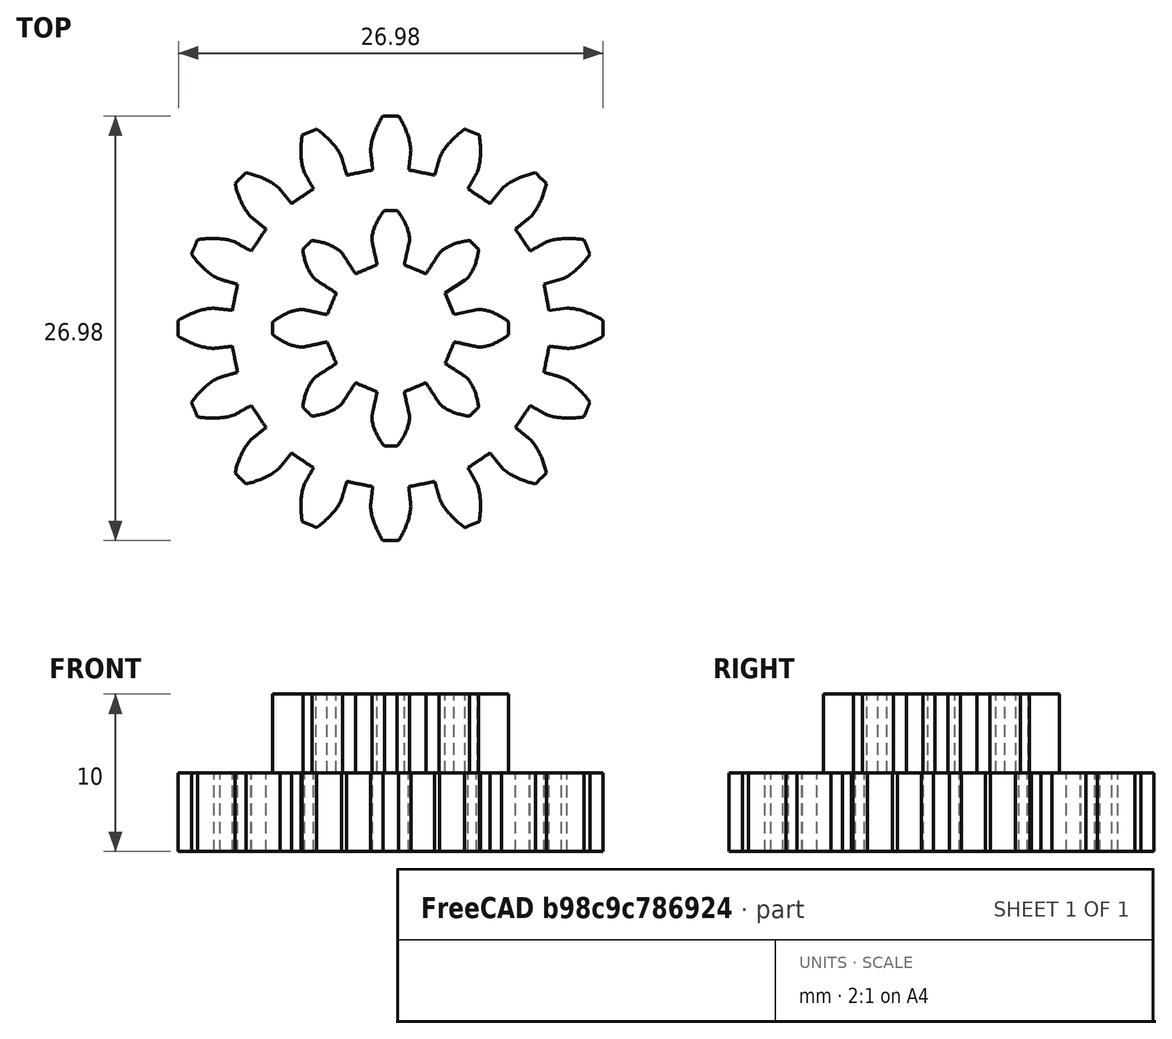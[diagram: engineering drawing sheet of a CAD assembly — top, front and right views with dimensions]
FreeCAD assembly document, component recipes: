
FREECAD ASSEMBLY — COMPONENT RECIPES ("smart_medication_box")

This assembly document has 6 components, labeled P0..P5 below (a component is one placed body or linked part). 6 of them carry a construction recipe — the FreeCAD feature program that regenerates the part from scratch, quoted from this document or its linked companion documents; the rest are supplied as boundary geometry only. No exploded tour is included for this assembly.
COMPONENT P0 — recipe-attached ("base", modeled in this document).
Construction recipe (the document's own serialized feature program — sketch geometry with constraints, then the solid features built on it; lengths are millimeters unless a unit is written):

FEATURE [Sketcher::SketchObject] Sketch003
  ArcFitTolerance = 1e-06
  AttachmentSupport = -> [Origin006]
  ExternalTypes = [0]
  FullyConstrained = true
  MakeInternals = false
  MapMode = 5
  expr: Constraints[0] = 53 * 2
  sketch-geometry (1):
    g0: Circle CenterX=0 CenterY=0 CenterZ=0 NormalX=0 NormalY=0 NormalZ=1 AngleXU=0 Radius=53
  constraints (2):
    c: Diameter(g0) = 106
    c: Coincident(g0,g-1)
FEATURE [PartDesign::Pad] Pad
  Direction = (0,0,1)
  Length = 6
  Length2 = 10
  Profile = -> Sketch003
  ReferenceAxis = -> Sketch003 [N_Axis]
  Refine = true
  SideType = 0
  Suppressed = false
  Type = 0
  Type2 = 0
  expr: Length = 6
FEATURE [Sketcher::SketchObject] Sketch004
  ArcFitTolerance = 1e-06
  AttachmentSupport = -> [Pad]
  ExternalTypes = [0]
  FullyConstrained = true
  MakeInternals = false
  MapMode = 5
  Placement = pos=(0,0,6) rot=(0,0,1;0rad)
  expr: Constraints[0] = 48 * 2 - 4
  sketch-geometry (1):
    g0: Circle CenterX=0 CenterY=0 CenterZ=0 NormalX=0 NormalY=0 NormalZ=1 AngleXU=0 Radius=46
  constraints (2):
    c: Diameter(g0) = 92
    c: Coincident(g0,g-1)
FEATURE [PartDesign::Pad] Pad001
  BaseFeature = -> Pad
  Direction = (0,0,1)
  Length = 6
  Length2 = 10
  Profile = -> Sketch004
  ReferenceAxis = -> Sketch004 [N_Axis]
  Refine = true
  SideType = 0
  Suppressed = false
  Type = 0
  Type2 = 0
  expr: Length = 6
FEATURE [Sketcher::SketchObject] Sketch005
  ArcFitTolerance = 1e-06
  AttachmentSupport = -> [Pad001]
  ExternalGeometry = -> [Pad001]
  ExternalTypes = [0]
  FullyConstrained = true
  MakeInternals = false
  MapMode = 5
  Placement = pos=(0,0,12) rot=(0,0,1;0rad)
  expr: Constraints[0] = 28
  expr: Constraints[4] = 11.5
  sketch-geometry (2):
    g0: Circle CenterX=34.5 CenterY=0 CenterZ=0 NormalX=0 NormalY=0 NormalZ=1 AngleXU=0 Radius=14
    g1: Circle [constr] CenterX=34.5 CenterY=0 CenterZ=0 NormalX=0 NormalY=0 NormalZ=1 AngleXU=0 Radius=11.5
  constraints (5):
    c: Diameter(g0) = 28
    c: Coincident(g1,g0)
    c: Tangent(g1,g-3)
    c: PointOnObject(g0,g-1)
    c: Distance(g0,g-3) = 11.5
FEATURE [PartDesign::Pocket] Pocket001
  BaseFeature = -> Pad001
  Direction = (0,0,-1)
  Length = 6
  Length2 = 5
  Profile = -> Sketch005
  ReferenceAxis = -> Sketch005 [N_Axis]
  Refine = true
  SideType = 0
  Suppressed = false
  Type = 0
  Type2 = 0
  expr: Length = 6
FEATURE [Sketcher::SketchObject] Sketch006
  ArcFitTolerance = 1e-06
  AttachmentSupport = -> [Pocket001]
  ExternalGeometry = -> [Pocket001]
  ExternalTypes = [0,0]
  FullyConstrained = true
  MakeInternals = false
  MapMode = 5
  Placement = pos=(0,0,6) rot=(0,0,1;0rad)
  sketch-geometry (1):
    g0: Circle CenterX=34.5 CenterY=0 CenterZ=0 NormalX=0 NormalY=0 NormalZ=1 AngleXU=0 Radius=7.6
  constraints (2):
    c: Diameter(g0) = 15.2
    c: Coincident(g0,g-4)
FEATURE [PartDesign::Pocket] Pocket002
  BaseFeature = -> Pocket001
  Direction = (0,0,-1)
  Length = 5
  Length2 = 5
  Profile = -> Sketch006
  ReferenceAxis = -> Sketch006 [N_Axis]
  Refine = true
  SideType = 0
  Suppressed = false
  Type = 0
  Type2 = 0
FEATURE [Sketcher::SketchObject] Sketch007
  ArcFitTolerance = 1e-06
  AttachmentSupport = -> [Pocket002]
  ExternalGeometry = -> [Pocket002]
  ExternalTypes = [0]
  FullyConstrained = true
  MakeInternals = false
  MapMode = 5
  Placement = pos=(0,0,12) rot=(0,0,1;0rad)
  expr: Constraints[0] = 28
  expr: Constraints[2] = -3
  sketch-geometry (1):
    g0: Circle CenterX=15.9 CenterY=0 CenterZ=0 NormalX=0 NormalY=0 NormalZ=1 AngleXU=0 Radius=14
  constraints (3):
    c: Diameter(g0) = 28
    c: PointOnObject(g0,g-1)
    c: Distance(g0,g-3) = -3
FEATURE [PartDesign::Pocket] Pocket003
  BaseFeature = -> Pocket002
  Direction = (0,0,-1)
  Length = 11
  Length2 = 5
  Profile = -> Sketch007
  ReferenceAxis = -> Sketch007 [N_Axis]
  Refine = true
  SideType = 0
  Suppressed = false
  Type = 0
  Type2 = 0
  expr: Length = 11
FEATURE [Part::DatumPlane] DatumPlane001
  AttachmentSupport = -> [Pocket003]
  MapMode = 7
  Placement = pos=(53,0,0) rot=(1,0,0;1.5708rad)
FEATURE [Sketcher::SketchObject] Sketch009
  ArcFitTolerance = 1e-06
  AttachmentSupport = -> [DatumPlane001]
  ExternalTypes = [0]
  FullyConstrained = false
  MakeInternals = false
  MapMode = 5
  Placement = pos=(53,0,0) rot=(1,0,0;1.5708rad)
  expr: Constraints[12] = 2
  expr: Constraints[2] = 6
  expr: Constraints[4] = 25
  sketch-geometry (17):
    g0: LineSegment StartX=0 StartY=0 StartZ=0 EndX=0 EndY=6 EndZ=0
    g1: LineSegment StartX=0 StartY=6 StartZ=0 EndX=24.3276 EndY=6 EndZ=0
    g2: LineSegment StartX=25.4755 StartY=6.47549 StartZ=0 EndX=26.6668 EndY=7.66678 EndZ=0
    g3: LineSegment StartX=27.4713 StartY=8 StartZ=0 EndX=28.4345 EndY=8 EndZ=0
    g4: LineSegment StartX=29 StartY=7.43449 StartZ=0 EndX=29 EndY=6.73331 EndZ=0
    g5: LineSegment StartX=28.4815 StartY=5.48147 StartZ=0 EndX=23.8351 EndY=0.835147 EndZ=0
    g6: LineSegment StartX=0 StartY=0 StartZ=0 EndX=21.8189 EndY=0 EndZ=0
    g7: ArcOfCircle CenterX=28.4345 CenterY=7.43449 CenterZ=0 NormalX=0 NormalY=0 NormalZ=1 AngleXU=0 Radius=0.565506 StartAngle=0 EndAngle=1.5708
    g8: GeomPoint [constr] X=29 Y=8 Z=0
    g9: ArcOfCircle CenterX=27.4713 CenterY=6.8623 CenterZ=0 NormalX=0 NormalY=0 NormalZ=1 AngleXU=0 Radius=1.1377 StartAngle=1.5708 EndAngle=2.35619
    g10: GeomPoint [constr] X=27 Y=8 Z=0
    g11: ArcOfCircle CenterX=27.2296 CenterY=6.73331 CenterZ=0 NormalX=0 NormalY=0 NormalZ=1 AngleXU=0 Radius=1.77037 StartAngle=5.49779 EndAngle=6.28319
    g12: GeomPoint [constr] X=29 Y=6 Z=0
    g13: ArcOfCircle CenterX=24.3276 CenterY=7.62341 CenterZ=0 NormalX=0 NormalY=0 NormalZ=1 AngleXU=0 Radius=1.62341 StartAngle=4.71239 EndAngle=5.49779
    g14: GeomPoint [constr] X=25 Y=6 Z=0
    g15: ArcOfCircle CenterX=21.8189 CenterY=2.85137 CenterZ=0 NormalX=0 NormalY=0 NormalZ=1 AngleXU=0 Radius=2.85137 StartAngle=4.71239 EndAngle=5.49779
    g16: GeomPoint [constr] X=23 Y=0 Z=0
  constraints (33):
    c: Coincident(g-1,g0)
    c: Coincident(g0,g1)
    c: Distance(g0,g0) = 6
    c: PointOnObject(g0,g-2)
    c: DistanceX(g1,g14) = 25
    c: PointOnObject(g16,g-1)
    c: Coincident(g6,g0)
    c: Parallel(g2,g5)
    c: Parallel(g1,g6)
    c: Parallel(g3,g1)
    c: Perpendicular(g3,g4)
    c: PointOnObject(g12,g1)
    c: DistanceY(g12,g8) = 2
    c: PointOnObject(g8,g3)
    c: PointOnObject(g8,g4)
    c: Tangent(g3,g7) = 1.5708
    c: Tangent(g4,g7) = 1.5708
    c: PointOnObject(g10,g2)
    c: PointOnObject(g10,g3)
    c: Tangent(g2,g9) = 1.5708
    c: Tangent(g3,g9) = 1.5708
    c: PointOnObject(g12,g5)
    c: PointOnObject(g12,g4)
    c: Tangent(g5,g11) = 1.5708
    c: Tangent(g4,g11) = 1.5708
    c: PointOnObject(g14,g2)
    c: PointOnObject(g14,g1)
    c: Tangent(g2,g13) = -1.5708
    c: Tangent(g1,g13) = -1.5708
    c: PointOnObject(g16,g5)
    c: PointOnObject(g16,g6)
    c: Tangent(g5,g15) = 1.5708
    c: Tangent(g6,g15) = -1.5708
FEATURE [PartDesign::Revolution] Revolution
  Angle = 360
  Angle2 = 60
  Axis = (1e-16,1e-16,1)
  Base = (0,0,0)
  BaseFeature = -> Pocket003
  Profile = -> Sketch009
  ReferenceAxis = -> Z_Axis003
  Refine = true
  Reversed = true
  Suppressed = false
  Type = 0
FEATURE [PartDesign::Fillet] Fillet
  Base = -> Revolution [Edge27]
  BaseFeature = -> Revolution
  Radius = 1
  Refine = true
  SupportTransform = false
  Suppressed = false
  UseAllEdges = false
FEATURE [Sketcher::SketchObject] Sketch019
  ArcFitTolerance = 1e-06
  AttachmentSupport = -> [Fillet]
  ExternalTypes = [0]
  FullyConstrained = true
  MakeInternals = false
  MapMode = 5
  Placement = pos=(0,0,12) rot=(0,0,1;0rad)
  sketch-geometry (1):
    g0: Circle CenterX=0 CenterY=0 CenterZ=0 NormalX=0 NormalY=0 NormalZ=1 AngleXU=0 Radius=44
  constraints (2):
    c: Diameter(g0) = 88
    c: Coincident(g0,g-1)
FEATURE [Part::DatumPlane] DatumPlane005
  AttachmentSupport = -> [Sketch019]
  MapMode = 7
  Placement = pos=(44,0,12) rot=(1,0,0;1.5708rad)
FEATURE [Sketcher::SketchObject] Sketch020
  ArcFitTolerance = 1e-06
  AttachmentSupport = -> [DatumPlane005]
  ExternalTypes = [0]
  FullyConstrained = true
  MakeInternals = false
  MapMode = 5
  Placement = pos=(44,0,12) rot=(1,0,0;1.5708rad)
  sketch-geometry (9):
    g0: LineSegment StartX=-2.19203 StartY=0 StartZ=0 EndX=-2.19203 EndY=3.1 EndZ=0
    g1: LineSegment StartX=-2.19203 StartY=3.1 StartZ=0 EndX=0 EndY=5.29203 EndZ=0
    g2: LineSegment StartX=0 StartY=5.29203 StartZ=0 EndX=0 EndY=7.79203 EndZ=0
    g3: LineSegment StartX=-5.9535 StartY=0 StartZ=0 EndX=-2.19203 EndY=0 EndZ=0
    g4: LineSegment StartX=0 StartY=7.79203 StartZ=0 EndX=-3.44203 EndY=4.35 EndZ=0
    g5: LineSegment StartX=-3.44203 StartY=4.35 StartZ=0 EndX=-5.9535 EndY=0 EndZ=0
    g6: LineSegment [constr] StartX=-3.44203 StartY=4.35 StartZ=0 EndX=-2.19203 EndY=3.1 EndZ=0
    g7: LineSegment StartX=-2.19203 StartY=0 StartZ=0 EndX=0 EndY=0 EndZ=0
    g8: LineSegment StartX=0 StartY=0 StartZ=0 EndX=0 EndY=5.29203 EndZ=0
  constraints (24):
    c: PointOnObject(g0,g-1)
    c: Vertical(g0)
    c: Coincident(g0,g1)
    c: PointOnObject(g1,g-2)
    c: Coincident(g1,g2)
    c: Coincident(g3,g0)
    c: PointOnObject(g3,g-1)
    c: PointOnObject(g2,g-2)
    c: Angle(g1,g0) = 0.785398
    c: DistanceY(g0,g0) = 3.1
    c: Equal(g1,g0)
    c: DistanceY(g2,g2) = 2.5
    c: Coincident(g2,g4)
    c: Coincident(g4,g5)
    c: Coincident(g3,g5)
    c: Angle(g3,g5) = 1.0472
    c: Parallel(g4,g1)
    c: Coincident(g6,g4)
    c: Coincident(g6,g0)
    c: Perpendicular(g4,g6)
    c: Coincident(g7,g0)
    c: Coincident(g7,g-1)
    c: Coincident(g8,g7)
    c: Coincident(g8,g1)
FEATURE [PartDesign::Revolution] Revolution005
  Angle = 323
  Angle2 = 47
  Axis = (1e-16,1e-16,1)
  Base = (0,0,0)
  BaseFeature = -> Fillet
  Profile = -> Sketch020 [Edge4,Edge5,Edge2,Edge1,Edge3,Edge6]
  ReferenceAxis = -> Z_Axis003
  Refine = true
  Reversed = true
  Suppressed = false
  Type = 4
  expr: Angle = 323
  expr: Angle2 = 47
FEATURE [PartDesign::Revolution] Revolution006
  Angle = 313
  Angle2 = 53
  Axis = (1e-16,1e-16,1)
  Base = (0,0,0)
  BaseFeature = -> Revolution005
  Profile = -> Sketch020 [Edge8,Edge3,Edge4,Edge5,Edge6,Edge7]
  ReferenceAxis = -> Z_Axis003
  Refine = true
  Reversed = true
  Suppressed = false
  Type = 4
  expr: Angle = 313
  expr: Angle2 = 53
FEATURE [PartDesign::PolarPattern] PolarPattern004
  Angle = 360
  Axis = -> Z_Axis003
  BaseFeature = -> Revolution006
  Mode = 0
  Occurrences = 4
  Offset = 120
  Originals = -> [Revolution005,Revolution006]
  Refine = true
  Suppressed = false
  TransformMode = 0
  expr: Occurrences = 4
FEATURE [PartDesign::Fillet] Fillet005
  Base = -> PolarPattern004 [Face58,Face22]
  BaseFeature = -> PolarPattern004
  Radius = 0.5
  Refine = true
  SupportTransform = false
  Suppressed = false
  UseAllEdges = false
  expr: Radius = 0.5
FEATURE [PartDesign::Fillet] Fillet006
  Base = -> Fillet005 [Face21,Face18]
  BaseFeature = -> Fillet005
  Radius = 0.5
  Refine = true
  SupportTransform = false
  Suppressed = false
  UseAllEdges = false
  expr: Radius = 0.5
FEATURE [PartDesign::Fillet] Fillet007
  Base = -> Fillet006 [Face29,Face32]
  BaseFeature = -> Fillet006
  Radius = 0.5
  Refine = true
  SupportTransform = false
  Suppressed = false
  UseAllEdges = false
FEATURE [PartDesign::Fillet] Fillet008
  Base = -> Fillet007 [Face44,Face41]
  BaseFeature = -> Fillet007
  Radius = 0.5
  Refine = true
  SupportTransform = false
  Suppressed = false
  UseAllEdges = false
FEATURE [PartDesign::Body] Body003
  AllowCompound = false
  Group = -> [Sketch003,Pad,Sketch004,Pad001,Sketch005,Pocket001,Sketch006,Pocket002,Sketch007,Pocket003,DatumPlane001,Sketch009,Revolution,Fillet,Sketch019,DatumPlane005,Sketch020,Revolution005,Revolution006,PolarPattern004,Fillet005,Fillet006,Fillet007,Fillet008]
  Origin = -> Origin006
  Tip = -> Fillet008
COMPONENT P1 — recipe-attached ("middle_gear", modeled in this document).
Construction recipe (the document's own serialized feature program — sketch geometry with constraints, then the solid features built on it; lengths are millimeters unless a unit is written):

FEATURE [PartDesign::Boolean] Boolean
  Group = -> [InvoluteGear003,InvoluteGear002,Body017]
  Suppressed = false
  Type = 0
  UsePlacement = true
FEATURE [PartDesign::Fillet] Fillet001
  Base = -> Boolean [Face4]
  BaseFeature = -> Boolean
  Radius = 0.25
  Refine = true
  SupportTransform = false
  Suppressed = false
  UseAllEdges = false
  expr: Radius = 0.25
FEATURE [PartDesign::Fillet] Fillet002
  Base = -> Fillet001 [Face4,Face243]
  BaseFeature = -> Fillet001
  Radius = 0.2
  Refine = true
  SupportTransform = false
  Suppressed = false
  UseAllEdges = false
  expr: Radius = 0.2
FEATURE [PartDesign::Body] Body018
  AllowCompound = false
  Group = -> [Boolean,Fillet001,Fillet002]
  Origin = -> Origin030
  Tip = -> Fillet002
COMPONENT P2 — recipe-attached ("desc_upper_ring", modeled in this document).
Construction recipe (the document's own serialized feature program — sketch geometry with constraints, then the solid features built on it; lengths are millimeters unless a unit is written):

FEATURE [Sketcher::SketchObject] Sketch021
  ArcFitTolerance = 1e-06
  AttachmentSupport = -> [Origin036]
  ExternalTypes = [0]
  FullyConstrained = true
  MakeInternals = false
  MapMode = 5
  expr: Constraints[2] = 42.75 * 2
  expr: Constraints[3] = 51 * 2
  sketch-geometry (2):
    g0: Circle CenterX=0 CenterY=0 CenterZ=0 NormalX=0 NormalY=0 NormalZ=1 AngleXU=0 Radius=42.75
    g1: Circle CenterX=0 CenterY=0 CenterZ=0 NormalX=0 NormalY=0 NormalZ=1 AngleXU=0 Radius=51
  constraints (4):
    c: Coincident(g0,g-1)
    c: Coincident(g1,g0)
    c: Diameter(g0) = 85.5
    c: Diameter(g1) = 102
FEATURE [PartDesign::Pad] Pad006
  Direction = (0,0,1)
  Length = 3
  Length2 = 10
  Profile = -> Sketch021
  ReferenceAxis = -> Sketch021 [N_Axis]
  Refine = true
  SideType = 0
  Suppressed = false
  Type = 0
  Type2 = 0
  expr: Length = 3
FEATURE [Sketcher::SketchObject] Sketch022
  ArcFitTolerance = 1e-06
  AttachmentSupport = -> [Pad006]
  ExternalTypes = [0]
  FullyConstrained = false
  MakeInternals = false
  MapMode = 5
  Placement = pos=(0,0,3) rot=(0,0,1;0rad)
  sketch-geometry (4):
    g0: ArcOfCircle CenterX=0 CenterY=0 CenterZ=0 NormalX=0 NormalY=0 NormalZ=1 AngleXU=0 Radius=44.0776 StartAngle=1.01451 EndAngle=1.42895
    g1: ArcOfCircle CenterX=0 CenterY=0 CenterZ=0 NormalX=0 NormalY=0 NormalZ=1 AngleXU=0 Radius=50.0776 StartAngle=1.01451 EndAngle=1.42895
    g2: LineSegment StartX=6.23147 StartY=43.6349 StartZ=0 EndX=7.07972 EndY=49.5746 EndZ=0
    g3: LineSegment StartX=23.2744 StartY=37.4317 StartZ=0 EndX=26.4426 EndY=42.5271 EndZ=0
  constraints (8):
    c: Coincident(g1,g0)
    c: Coincident(g2,g0)
    c: Coincident(g2,g1)
    c: Coincident(g3,g0)
    c: Coincident(g3,g1)
    c: Equal(g2,g3)
    c: Perpendicular(g0,g2)
    c: Distance(g3,g3) = 6
FEATURE [PartDesign::Pocket] Pocket006
  BaseFeature = -> Pad006
  Direction = (0,0,-1)
  Length = 1.5
  Length2 = 5
  Profile = -> Sketch022
  ReferenceAxis = -> Sketch022 [N_Axis]
  Refine = true
  SideType = 0
  Suppressed = false
  Type = 0
  Type2 = 0
  expr: Length = 1.5
FEATURE [PartDesign::PolarPattern] PolarPattern005
  Angle = 360
  Axis = -> Sketch022 [N_Axis]
  BaseFeature = -> Pocket006
  Mode = 0
  Occurrences = 2
  Offset = 120
  Originals = -> [Pocket006]
  Refine = true
  Suppressed = false
  TransformMode = 0
FEATURE [PartDesign::Fillet] Fillet010
  Base = -> PolarPattern005 [Face2]
  BaseFeature = -> PolarPattern005
  Radius = 0.3
  Refine = true
  SupportTransform = false
  Suppressed = false
  UseAllEdges = false
  expr: Radius = 0.3
FEATURE [PartDesign::Fillet] Fillet011
  Base = -> Fillet010 [Face3]
  BaseFeature = -> Fillet010
  Radius = 0.4
  Refine = true
  SupportTransform = false
  Suppressed = false
  UseAllEdges = false
  expr: Radius = 0.4
FEATURE [Sketcher::SketchObject] Sketch023
  ArcFitTolerance = 1e-06
  AttachmentSupport = -> [Fillet011]
  ExternalTypes = [0]
  FullyConstrained = false
  MakeInternals = false
  MapMode = 5
  Placement = pos=(0,0,0) rot=(1,0,0;3.14159rad)
  sketch-geometry (1190):
    g0: BSplineCurve PolesCount=2 KnotsCount=2 Degree=1 IsPeriodic=0
    g1: BSplineCurve PolesCount=2 KnotsCount=2 Degree=1 IsPeriodic=0
    g2: BSplineCurve PolesCount=2 KnotsCount=2 Degree=1 IsPeriodic=0
    g3: BSplineCurve PolesCount=2 KnotsCount=2 Degree=1 IsPeriodic=0
    g4: BSplineCurve PolesCount=2 KnotsCount=2 Degree=1 IsPeriodic=0
    g5: BSplineCurve PolesCount=2 KnotsCount=2 Degree=1 IsPeriodic=0
    g6: BSplineCurve PolesCount=2 KnotsCount=2 Degree=1 IsPeriodic=0
    g7: BSplineCurve PolesCount=2 KnotsCount=2 Degree=1 IsPeriodic=0
    g8: BSplineCurve PolesCount=2 KnotsCount=2 Degree=1 IsPeriodic=0
    g9: BSplineCurve PolesCount=2 KnotsCount=2 Degree=1 IsPeriodic=0
    g10: BSplineCurve PolesCount=2 KnotsCount=2 Degree=1 IsPeriodic=0
    g11: BSplineCurve PolesCount=2 KnotsCount=2 Degree=1 IsPeriodic=0
    g12: BSplineCurve PolesCount=2 KnotsCount=2 Degree=1 IsPeriodic=0
    g13: BSplineCurve PolesCount=2 KnotsCount=2 Degree=1 IsPeriodic=0
    g14: BSplineCurve PolesCount=2 KnotsCount=2 Degree=1 IsPeriodic=0
    g15: BSplineCurve PolesCount=2 KnotsCount=2 Degree=1 IsPeriodic=0
    g16: BSplineCurve PolesCount=2 KnotsCount=2 Degree=1 IsPeriodic=0
    g17: BSplineCurve PolesCount=2 KnotsCount=2 Degree=1 IsPeriodic=0
    g18: BSplineCurve PolesCount=2 KnotsCount=2 Degree=1 IsPeriodic=0
    g19: BSplineCurve PolesCount=2 KnotsCount=2 Degree=1 IsPeriodic=0
    g20: BSplineCurve PolesCount=2 KnotsCount=2 Degree=1 IsPeriodic=0
    g21: BSplineCurve PolesCount=2 KnotsCount=2 Degree=1 IsPeriodic=0
    g22: BSplineCurve PolesCount=2 KnotsCount=2 Degree=1 IsPeriodic=0
    g23: BSplineCurve PolesCount=2 KnotsCount=2 Degree=1 IsPeriodic=0
    g24: BSplineCurve PolesCount=2 KnotsCount=2 Degree=1 IsPeriodic=0
    g25: BSplineCurve PolesCount=2 KnotsCount=2 Degree=1 IsPeriodic=0
    g26: BSplineCurve PolesCount=2 KnotsCount=2 Degree=1 IsPeriodic=0
    g27: BSplineCurve PolesCount=2 KnotsCount=2 Degree=1 IsPeriodic=0
    g28: BSplineCurve PolesCount=2 KnotsCount=2 Degree=1 IsPeriodic=0
    g29: BSplineCurve PolesCount=2 KnotsCount=2 Degree=1 IsPeriodic=0
    g30: BSplineCurve PolesCount=2 KnotsCount=2 Degree=1 IsPeriodic=0
    g31: BSplineCurve PolesCount=2 KnotsCount=2 Degree=1 IsPeriodic=0
    g32: BSplineCurve PolesCount=2 KnotsCount=2 Degree=1 IsPeriodic=0
    g33: BSplineCurve PolesCount=2 KnotsCount=2 Degree=1 IsPeriodic=0
    g34: BSplineCurve PolesCount=2 KnotsCount=2 Degree=1 IsPeriodic=0
    g35: BSplineCurve PolesCount=2 KnotsCount=2 Degree=1 IsPeriodic=0
    g36: BSplineCurve PolesCount=2 KnotsCount=2 Degree=1 IsPeriodic=0
    g37: BSplineCurve PolesCount=2 KnotsCount=2 Degree=1 IsPeriodic=0
    g38: BSplineCurve PolesCount=2 KnotsCount=2 Degree=1 IsPeriodic=0
    g39: BSplineCurve PolesCount=2 KnotsCount=2 Degree=1 IsPeriodic=0
    g40: BSplineCurve PolesCount=2 KnotsCount=2 Degree=1 IsPeriodic=0
    g41: BSplineCurve PolesCount=2 KnotsCount=2 Degree=1 IsPeriodic=0
    g42: BSplineCurve PolesCount=2 KnotsCount=2 Degree=1 IsPeriodic=0
    g43: BSplineCurve PolesCount=2 KnotsCount=2 Degree=1 IsPeriodic=0
    g44: BSplineCurve PolesCount=2 KnotsCount=2 Degree=1 IsPeriodic=0
    g45: BSplineCurve PolesCount=2 KnotsCount=2 Degree=1 IsPeriodic=0
    g46: BSplineCurve PolesCount=2 KnotsCount=2 Degree=1 IsPeriodic=0
    g47: BSplineCurve PolesCount=2 KnotsCount=2 Degree=1 IsPeriodic=0
    g48: BSplineCurve PolesCount=2 KnotsCount=2 Degree=1 IsPeriodic=0
    g49: BSplineCurve PolesCount=2 KnotsCount=2 Degree=1 IsPeriodic=0
    g50: BSplineCurve PolesCount=2 KnotsCount=2 Degree=1 IsPeriodic=0
    g51: BSplineCurve PolesCount=2 KnotsCount=2 Degree=1 IsPeriodic=0
    g52: BSplineCurve PolesCount=2 KnotsCount=2 Degree=1 IsPeriodic=0
    g53: BSplineCurve PolesCount=2 KnotsCount=2 Degree=1 IsPeriodic=0
    g54: BSplineCurve PolesCount=2 KnotsCount=2 Degree=1 IsPeriodic=0
    g55: BSplineCurve PolesCount=2 KnotsCount=2 Degree=1 IsPeriodic=0
    g56: BSplineCurve PolesCount=2 KnotsCount=2 Degree=1 IsPeriodic=0
    g57: BSplineCurve PolesCount=2 KnotsCount=2 Degree=1 IsPeriodic=0
    g58: BSplineCurve PolesCount=2 KnotsCount=2 Degree=1 IsPeriodic=0
    g59: BSplineCurve PolesCount=2 KnotsCount=2 Degree=1 IsPeriodic=0
    g60: BSplineCurve PolesCount=2 KnotsCount=2 Degree=1 IsPeriodic=0
    g61: BSplineCurve PolesCount=2 KnotsCount=2 Degree=1 IsPeriodic=0
    g62: BSplineCurve PolesCount=2 KnotsCount=2 Degree=1 IsPeriodic=0
    g63: BSplineCurve PolesCount=2 KnotsCount=2 Degree=1 IsPeriodic=0
    g64: BSplineCurve PolesCount=2 KnotsCount=2 Degree=1 IsPeriodic=0
    g65: BSplineCurve PolesCount=2 KnotsCount=2 Degree=1 IsPeriodic=0
    g66: BSplineCurve PolesCount=2 KnotsCount=2 Degree=1 IsPeriodic=0
    g67: BSplineCurve PolesCount=2 KnotsCount=2 Degree=1 IsPeriodic=0
    g68: BSplineCurve PolesCount=2 KnotsCount=2 Degree=1 IsPeriodic=0
    g69: BSplineCurve PolesCount=2 KnotsCount=2 Degree=1 IsPeriodic=0
    g70: BSplineCurve PolesCount=2 KnotsCount=2 Degree=1 IsPeriodic=0
    g71: BSplineCurve PolesCount=2 KnotsCount=2 Degree=1 IsPeriodic=0
    g72: BSplineCurve PolesCount=2 KnotsCount=2 Degree=1 IsPeriodic=0
    g73: BSplineCurve PolesCount=2 KnotsCount=2 Degree=1 IsPeriodic=0
    g74: BSplineCurve PolesCount=2 KnotsCount=2 Degree=1 IsPeriodic=0
    g75: BSplineCurve PolesCount=2 KnotsCount=2 Degree=1 IsPeriodic=0
    g76: BSplineCurve PolesCount=2 KnotsCount=2 Degree=1 IsPeriodic=0
    g77: BSplineCurve PolesCount=2 KnotsCount=2 Degree=1 IsPeriodic=0
    g78: BSplineCurve PolesCount=2 KnotsCount=2 Degree=1 IsPeriodic=0
    g79: BSplineCurve PolesCount=2 KnotsCount=2 Degree=1 IsPeriodic=0
    g80: BSplineCurve PolesCount=2 KnotsCount=2 Degree=1 IsPeriodic=0
    g81: BSplineCurve PolesCount=2 KnotsCount=2 Degree=1 IsPeriodic=0
    g82: BSplineCurve PolesCount=2 KnotsCount=2 Degree=1 IsPeriodic=0
    g83: BSplineCurve PolesCount=2 KnotsCount=2 Degree=1 IsPeriodic=0
    g84: BSplineCurve PolesCount=2 KnotsCount=2 Degree=1 IsPeriodic=0
    g85: BSplineCurve PolesCount=2 KnotsCount=2 Degree=1 IsPeriodic=0
    g86: BSplineCurve PolesCount=2 KnotsCount=2 Degree=1 IsPeriodic=0
    g87: BSplineCurve PolesCount=2 KnotsCount=2 Degree=1 IsPeriodic=0
    g88: BSplineCurve PolesCount=2 KnotsCount=2 Degree=1 IsPeriodic=0
    g89: BSplineCurve PolesCount=2 KnotsCount=2 Degree=1 IsPeriodic=0
    g90: BSplineCurve PolesCount=2 KnotsCount=2 Degree=1 IsPeriodic=0
    g91: BSplineCurve PolesCount=2 KnotsCount=2 Degree=1 IsPeriodic=0
    g92: BSplineCurve PolesCount=2 KnotsCount=2 Degree=1 IsPeriodic=0
    g93: BSplineCurve PolesCount=2 KnotsCount=2 Degree=1 IsPeriodic=0
    g94: BSplineCurve PolesCount=2 KnotsCount=2 Degree=1 IsPeriodic=0
    g95: BSplineCurve PolesCount=2 KnotsCount=2 Degree=1 IsPeriodic=0
    g96: BSplineCurve PolesCount=2 KnotsCount=2 Degree=1 IsPeriodic=0
    g97: BSplineCurve PolesCount=2 KnotsCount=2 Degree=1 IsPeriodic=0
    g98: BSplineCurve PolesCount=2 KnotsCount=2 Degree=1 IsPeriodic=0
    g99: BSplineCurve PolesCount=2 KnotsCount=2 Degree=1 IsPeriodic=0
    g100: BSplineCurve PolesCount=2 KnotsCount=2 Degree=1 IsPeriodic=0
    g101: BSplineCurve PolesCount=2 KnotsCount=2 Degree=1 IsPeriodic=0
    g102: BSplineCurve PolesCount=2 KnotsCount=2 Degree=1 IsPeriodic=0
    g103: BSplineCurve PolesCount=2 KnotsCount=2 Degree=1 IsPeriodic=0
    g104: BSplineCurve PolesCount=2 KnotsCount=2 Degree=1 IsPeriodic=0
    g105: BSplineCurve PolesCount=2 KnotsCount=2 Degree=1 IsPeriodic=0
    g106: BSplineCurve PolesCount=2 KnotsCount=2 Degree=1 IsPeriodic=0
    g107: BSplineCurve PolesCount=2 KnotsCount=2 Degree=1 IsPeriodic=0
    g108: BSplineCurve PolesCount=2 KnotsCount=2 Degree=1 IsPeriodic=0
    g109: BSplineCurve PolesCount=2 KnotsCount=2 Degree=1 IsPeriodic=0
    g110: BSplineCurve PolesCount=2 KnotsCount=2 Degree=1 IsPeriodic=0
    g111: BSplineCurve PolesCount=2 KnotsCount=2 Degree=1 IsPeriodic=0
    g112: BSplineCurve PolesCount=2 KnotsCount=2 Degree=1 IsPeriodic=0
    g113: BSplineCurve PolesCount=2 KnotsCount=2 Degree=1 IsPeriodic=0
    g114: BSplineCurve PolesCount=2 KnotsCount=2 Degree=1 IsPeriodic=0
    g115: BSplineCurve PolesCount=2 KnotsCount=2 Degree=1 IsPeriodic=0
    g116: BSplineCurve PolesCount=2 KnotsCount=2 Degree=1 IsPeriodic=0
    g117: BSplineCurve PolesCount=2 KnotsCount=2 Degree=1 IsPeriodic=0
    g118: BSplineCurve PolesCount=2 KnotsCount=2 Degree=1 IsPeriodic=0
    g119: BSplineCurve PolesCount=2 KnotsCount=2 Degree=1 IsPeriodic=0
    g120: BSplineCurve PolesCount=2 KnotsCount=2 Degree=1 IsPeriodic=0
    g121: BSplineCurve PolesCount=2 KnotsCount=2 Degree=1 IsPeriodic=0
    g122: BSplineCurve PolesCount=2 KnotsCount=2 Degree=1 IsPeriodic=0
    g123: BSplineCurve PolesCount=2 KnotsCount=2 Degree=1 IsPeriodic=0
    g124: BSplineCurve PolesCount=2 KnotsCount=2 Degree=1 IsPeriodic=0
    g125: BSplineCurve PolesCount=2 KnotsCount=2 Degree=1 IsPeriodic=0
    g126: BSplineCurve PolesCount=2 KnotsCount=2 Degree=1 IsPeriodic=0
    g127: BSplineCurve PolesCount=2 KnotsCount=2 Degree=1 IsPeriodic=0
    g128: BSplineCurve PolesCount=3 KnotsCount=2 Degree=2 IsPeriodic=0
    g129: BSplineCurve PolesCount=3 KnotsCount=2 Degree=2 IsPeriodic=0
    g130: BSplineCurve PolesCount=3 KnotsCount=2 Degree=2 IsPeriodic=0
    g131: BSplineCurve PolesCount=3 KnotsCount=2 Degree=2 IsPeriodic=0
    g132: BSplineCurve PolesCount=3 KnotsCount=2 Degree=2 IsPeriodic=0
    g133: BSplineCurve PolesCount=3 KnotsCount=2 Degree=2 IsPeriodic=0
    g134: BSplineCurve PolesCount=3 KnotsCount=2 Degree=2 IsPeriodic=0
    g135: BSplineCurve PolesCount=3 KnotsCount=2 Degree=2 IsPeriodic=0
    g136: BSplineCurve PolesCount=3 KnotsCount=2 Degree=2 IsPeriodic=0
    g137: BSplineCurve PolesCount=3 KnotsCount=2 Degree=2 IsPeriodic=0
    g138: BSplineCurve PolesCount=3 KnotsCount=2 Degree=2 IsPeriodic=0
    g139: BSplineCurve PolesCount=3 KnotsCount=2 Degree=2 IsPeriodic=0
    g140: BSplineCurve PolesCount=3 KnotsCount=2 Degree=2 IsPeriodic=0
    g141: BSplineCurve PolesCount=3 KnotsCount=2 Degree=2 IsPeriodic=0
    g142: BSplineCurve PolesCount=3 KnotsCount=2 Degree=2 IsPeriodic=0
    g143: BSplineCurve PolesCount=3 KnotsCount=2 Degree=2 IsPeriodic=0
    g144: BSplineCurve PolesCount=2 KnotsCount=2 Degree=1 IsPeriodic=0
    g145: BSplineCurve PolesCount=2 KnotsCount=2 Degree=1 IsPeriodic=0
    g146: BSplineCurve PolesCount=2 KnotsCount=2 Degree=1 IsPeriodic=0
    g147: BSplineCurve PolesCount=2 KnotsCount=2 Degree=1 IsPeriodic=0
    g148: BSplineCurve PolesCount=2 KnotsCount=2 Degree=1 IsPeriodic=0
    g149: BSplineCurve PolesCount=2 KnotsCount=2 Degree=1 IsPeriodic=0
    g150: BSplineCurve PolesCount=2 KnotsCount=2 Degree=1 IsPeriodic=0
    g151: BSplineCurve PolesCount=2 KnotsCount=2 Degree=1 IsPeriodic=0
    g152: BSplineCurve PolesCount=2 KnotsCount=2 Degree=1 IsPeriodic=0
    g153: BSplineCurve PolesCount=2 KnotsCount=2 Degree=1 IsPeriodic=0
    g154: BSplineCurve PolesCount=2 KnotsCount=2 Degree=1 IsPeriodic=0
    g155: BSplineCurve PolesCount=2 KnotsCount=2 Degree=1 IsPeriodic=0
    g156: BSplineCurve PolesCount=3 KnotsCount=2 Degree=2 IsPeriodic=0
    g157: BSplineCurve PolesCount=3 KnotsCount=2 Degree=2 IsPeriodic=0
    g158: BSplineCurve PolesCount=3 KnotsCount=2 Degree=2 IsPeriodic=0
    g159: BSplineCurve PolesCount=3 KnotsCount=2 Degree=2 IsPeriodic=0
    g160: BSplineCurve PolesCount=3 KnotsCount=2 Degree=2 IsPeriodic=0
    g161: BSplineCurve PolesCount=3 KnotsCount=2 Degree=2 IsPeriodic=0
    g162: BSplineCurve PolesCount=3 KnotsCount=2 Degree=2 IsPeriodic=0
    g163: BSplineCurve PolesCount=3 KnotsCount=2 Degree=2 IsPeriodic=0
    g164: BSplineCurve PolesCount=3 KnotsCount=2 Degree=2 IsPeriodic=0
    g165: BSplineCurve PolesCount=3 KnotsCount=2 Degree=2 IsPeriodic=0
    g166: BSplineCurve PolesCount=2 KnotsCount=2 Degree=1 IsPeriodic=0
    g167: BSplineCurve PolesCount=3 KnotsCount=2 Degree=2 IsPeriodic=0
    g168: BSplineCurve PolesCount=3 KnotsCount=2 Degree=2 IsPeriodic=0
    g169: BSplineCurve PolesCount=3 KnotsCount=2 Degree=2 IsPeriodic=0
    g170: BSplineCurve PolesCount=3 KnotsCount=2 Degree=2 IsPeriodic=0
    g171: BSplineCurve PolesCount=3 KnotsCount=2 Degree=2 IsPeriodic=0
    g172: BSplineCurve PolesCount=3 KnotsCount=2 Degree=2 IsPeriodic=0
    g173: BSplineCurve PolesCount=3 KnotsCount=2 Degree=2 IsPeriodic=0
    g174: BSplineCurve PolesCount=3 KnotsCount=2 Degree=2 IsPeriodic=0
    g175: BSplineCurve PolesCount=3 KnotsCount=2 Degree=2 IsPeriodic=0
    g176: BSplineCurve PolesCount=2 KnotsCount=2 Degree=1 IsPeriodic=0
    g177: BSplineCurve PolesCount=2 KnotsCount=2 Degree=1 IsPeriodic=0
    g178: BSplineCurve PolesCount=2 KnotsCount=2 Degree=1 IsPeriodic=0
    g179: BSplineCurve PolesCount=3 KnotsCount=2 Degree=2 IsPeriodic=0
    g180: BSplineCurve PolesCount=3 KnotsCount=2 Degree=2 IsPeriodic=0
    g181: BSplineCurve PolesCount=3 KnotsCount=2 Degree=2 IsPeriodic=0
    g182: BSplineCurve PolesCount=3 KnotsCount=2 Degree=2 IsPeriodic=0
    g183: BSplineCurve PolesCount=2 KnotsCount=2 Degree=1 IsPeriodic=0
    g184: BSplineCurve PolesCount=3 KnotsCount=2 Degree=2 IsPeriodic=0
    g185: BSplineCurve PolesCount=3 KnotsCount=2 Degree=2 IsPeriodic=0
    g186: BSplineCurve PolesCount=3 KnotsCount=2 Degree=2 IsPeriodic=0
    g187: BSplineCurve PolesCount=3 KnotsCount=2 Degree=2 IsPeriodic=0
    g188: BSplineCurve PolesCount=3 KnotsCount=2 Degree=2 IsPeriodic=0
    g189: BSplineCurve PolesCount=2 KnotsCount=2 Degree=1 IsPeriodic=0
    g190: BSplineCurve PolesCount=2 KnotsCount=2 Degree=1 IsPeriodic=0
    g191: BSplineCurve PolesCount=2 KnotsCount=2 Degree=1 IsPeriodic=0
    g192: BSplineCurve PolesCount=3 KnotsCount=2 Degree=2 IsPeriodic=0
    g193: BSplineCurve PolesCount=3 KnotsCount=2 Degree=2 IsPeriodic=0
    g194: BSplineCurve PolesCount=3 KnotsCount=2 Degree=2 IsPeriodic=0
    g195: BSplineCurve PolesCount=3 KnotsCount=2 Degree=2 IsPeriodic=0
    g196: BSplineCurve PolesCount=3 KnotsCount=2 Degree=2 IsPeriodic=0
    g197: BSplineCurve PolesCount=3 KnotsCount=2 Degree=2 IsPeriodic=0
    g198: BSplineCurve PolesCount=2 KnotsCount=2 Degree=1 IsPeriodic=0
    g199: BSplineCurve PolesCount=3 KnotsCount=2 Degree=2 IsPeriodic=0
    g200: BSplineCurve PolesCount=3 KnotsCount=2 Degree=2 IsPeriodic=0
    g201: BSplineCurve PolesCount=3 KnotsCount=2 Degree=2 IsPeriodic=0
    g202: BSplineCurve PolesCount=3 KnotsCount=2 Degree=2 IsPeriodic=0
    g203: BSplineCurve PolesCount=3 KnotsCount=2 Degree=2 IsPeriodic=0
    g204: BSplineCurve PolesCount=3 KnotsCount=2 Degree=2 IsPeriodic=0
    g205: BSplineCurve PolesCount=2 KnotsCount=2 Degree=1 IsPeriodic=0
    g206: BSplineCurve PolesCount=3 KnotsCount=2 Degree=2 IsPeriodic=0
    g207: BSplineCurve PolesCount=3 KnotsCount=2 Degree=2 IsPeriodic=0
    g208: BSplineCurve PolesCount=2 KnotsCount=2 Degree=1 IsPeriodic=0
    g209: BSplineCurve PolesCount=2 KnotsCount=2 Degree=1 IsPeriodic=0
    g210: BSplineCurve PolesCount=2 KnotsCount=2 Degree=1 IsPeriodic=0
    g211: BSplineCurve PolesCount=2 KnotsCount=2 Degree=1 IsPeriodic=0
    g212: BSplineCurve PolesCount=2 KnotsCount=2 Degree=1 IsPeriodic=0
    g213: BSplineCurve PolesCount=2 KnotsCount=2 Degree=1 IsPeriodic=0
    g214: BSplineCurve PolesCount=2 KnotsCount=2 Degree=1 IsPeriodic=0
    g215: BSplineCurve PolesCount=2 KnotsCount=2 Degree=1 IsPeriodic=0
    g216: BSplineCurve PolesCount=2 KnotsCount=2 Degree=1 IsPeriodic=0
    g217: BSplineCurve PolesCount=2 KnotsCount=2 Degree=1 IsPeriodic=0
    g218: BSplineCurve PolesCount=2 KnotsCount=2 Degree=1 IsPeriodic=0
    g219: BSplineCurve PolesCount=2 KnotsCount=2 Degree=1 IsPeriodic=0
    g220: BSplineCurve PolesCount=2 KnotsCount=2 Degree=1 IsPeriodic=0
    g221: BSplineCurve PolesCount=2 KnotsCount=2 Degree=1 IsPeriodic=0
    g222: BSplineCurve PolesCount=2 KnotsCount=2 Degree=1 IsPeriodic=0
    g223: BSplineCurve PolesCount=2 KnotsCount=2 Degree=1 IsPeriodic=0
    g224: BSplineCurve PolesCount=3 KnotsCount=2 Degree=2 IsPeriodic=0
    g225: BSplineCurve PolesCount=3 KnotsCount=2 Degree=2 IsPeriodic=0
    g226: BSplineCurve PolesCount=3 KnotsCount=2 Degree=2 IsPeriodic=0
    g227: BSplineCurve PolesCount=3 KnotsCount=2 Degree=2 IsPeriodic=0
    g228: BSplineCurve PolesCount=3 KnotsCount=2 Degree=2 IsPeriodic=0
    g229: BSplineCurve PolesCount=3 KnotsCount=2 Degree=2 IsPeriodic=0
    g230: BSplineCurve PolesCount=2 KnotsCount=2 Degree=1 IsPeriodic=0
    g231: BSplineCurve PolesCount=3 KnotsCount=2 Degree=2 IsPeriodic=0
    g232: BSplineCurve PolesCount=3 KnotsCount=2 Degree=2 IsPeriodic=0
    g233: BSplineCurve PolesCount=3 KnotsCount=2 Degree=2 IsPeriodic=0
    g234: BSplineCurve PolesCount=3 KnotsCount=2 Degree=2 IsPeriodic=0
    g235: BSplineCurve PolesCount=3 KnotsCount=2 Degree=2 IsPeriodic=0
    g236: BSplineCurve PolesCount=3 KnotsCount=2 Degree=2 IsPeriodic=0
    g237: BSplineCurve PolesCount=3 KnotsCount=2 Degree=2 IsPeriodic=0
    g238: BSplineCurve PolesCount=2 KnotsCount=2 Degree=1 IsPeriodic=0
    g239: BSplineCurve PolesCount=2 KnotsCount=2 Degree=1 IsPeriodic=0
    g240: BSplineCurve PolesCount=2 KnotsCount=2 Degree=1 IsPeriodic=0
    g241: BSplineCurve PolesCount=2 KnotsCount=2 Degree=1 IsPeriodic=0
    g242: BSplineCurve PolesCount=2 KnotsCount=2 Degree=1 IsPeriodic=0
    g243: BSplineCurve PolesCount=2 KnotsCount=2 Degree=1 IsPeriodic=0
    g244: BSplineCurve PolesCount=3 KnotsCount=2 Degree=2 IsPeriodic=0
    g245: BSplineCurve PolesCount=3 KnotsCount=2 Degree=2 IsPeriodic=0
    g246: BSplineCurve PolesCount=3 KnotsCount=2 Degree=2 IsPeriodic=0
    g247: BSplineCurve PolesCount=3 KnotsCount=2 Degree=2 IsPeriodic=0
    g248: BSplineCurve PolesCount=3 KnotsCount=2 Degree=2 IsPeriodic=0
    g249: BSplineCurve PolesCount=3 KnotsCount=2 Degree=2 IsPeriodic=0
    g250: BSplineCurve PolesCount=3 KnotsCount=2 Degree=2 IsPeriodic=0
    g251: BSplineCurve PolesCount=3 KnotsCount=2 Degree=2 IsPeriodic=0
    g252: BSplineCurve PolesCount=3 KnotsCount=2 Degree=2 IsPeriodic=0
    g253: BSplineCurve PolesCount=3 KnotsCount=2 Degree=2 IsPeriodic=0
    g254: BSplineCurve PolesCount=3 KnotsCount=2 Degree=2 IsPeriodic=0
    g255: BSplineCurve PolesCount=3 KnotsCount=2 Degree=2 IsPeriodic=0
    g256: BSplineCurve PolesCount=3 KnotsCount=2 Degree=2 IsPeriodic=0
    g257: BSplineCurve PolesCount=3 KnotsCount=2 Degree=2 IsPeriodic=0
    g258: BSplineCurve PolesCount=3 KnotsCount=2 Degree=2 IsPeriodic=0
    g259: BSplineCurve PolesCount=3 KnotsCount=2 Degree=2 IsPeriodic=0
    g260: BSplineCurve PolesCount=3 KnotsCount=2 Degree=2 IsPeriodic=0
    g261: BSplineCurve PolesCount=2 KnotsCount=2 Degree=1 IsPeriodic=0
    g262: BSplineCurve PolesCount=3 KnotsCount=2 Degree=2 IsPeriodic=0
    g263: BSplineCurve PolesCount=3 KnotsCount=2 Degree=2 IsPeriodic=0
    g264: BSplineCurve PolesCount=3 KnotsCount=2 Degree=2 IsPeriodic=0
    g265: BSplineCurve PolesCount=3 KnotsCount=2 Degree=2 IsPeriodic=0
    g266: BSplineCurve PolesCount=3 KnotsCount=2 Degree=2 IsPeriodic=0
    g267: BSplineCurve PolesCount=3 KnotsCount=2 Degree=2 IsPeriodic=0
    g268: BSplineCurve PolesCount=3 KnotsCount=2 Degree=2 IsPeriodic=0
    g269: BSplineCurve PolesCount=3 KnotsCount=2 Degree=2 IsPeriodic=0
    g270: BSplineCurve PolesCount=3 KnotsCount=2 Degree=2 IsPeriodic=0
    g271: BSplineCurve PolesCount=3 KnotsCount=2 Degree=2 IsPeriodic=0
    g272: BSplineCurve PolesCount=3 KnotsCount=2 Degree=2 IsPeriodic=0
    g273: BSplineCurve PolesCount=2 KnotsCount=2 Degree=1 IsPeriodic=0
    g274: BSplineCurve PolesCount=3 KnotsCount=2 Degree=2 IsPeriodic=0
    g275: BSplineCurve PolesCount=3 KnotsCount=2 Degree=2 IsPeriodic=0
    g276: BSplineCurve PolesCount=2 KnotsCount=2 Degree=1 IsPeriodic=0
    g277: BSplineCurve PolesCount=2 KnotsCount=2 Degree=1 IsPeriodic=0
    g278: BSplineCurve PolesCount=2 KnotsCount=2 Degree=1 IsPeriodic=0
    g279: BSplineCurve PolesCount=2 KnotsCount=2 Degree=1 IsPeriodic=0
    g280: BSplineCurve PolesCount=3 KnotsCount=2 Degree=2 IsPeriodic=0
    g281: BSplineCurve PolesCount=3 KnotsCount=2 Degree=2 IsPeriodic=0
    g282: BSplineCurve PolesCount=3 KnotsCount=2 Degree=2 IsPeriodic=0
    g283: BSplineCurve PolesCount=3 KnotsCount=2 Degree=2 IsPeriodic=0
    g284: BSplineCurve PolesCount=3 KnotsCount=2 Degree=2 IsPeriodic=0
    g285: BSplineCurve PolesCount=2 KnotsCount=2 Degree=1 IsPeriodic=0
    g286: BSplineCurve PolesCount=3 KnotsCount=2 Degree=2 IsPeriodic=0
    g287: BSplineCurve PolesCount=3 KnotsCount=2 Degree=2 IsPeriodic=0
    g288: BSplineCurve PolesCount=3 KnotsCount=2 Degree=2 IsPeriodic=0
    g289: BSplineCurve PolesCount=3 KnotsCount=2 Degree=2 IsPeriodic=0
    g290: BSplineCurve PolesCount=3 KnotsCount=2 Degree=2 IsPeriodic=0
    g291: BSplineCurve PolesCount=3 KnotsCount=2 Degree=2 IsPeriodic=0
    g292: BSplineCurve PolesCount=2 KnotsCount=2 Degree=1 IsPeriodic=0
    g293: BSplineCurve PolesCount=3 KnotsCount=2 Degree=2 IsPeriodic=0
    g294: BSplineCurve PolesCount=3 KnotsCount=2 Degree=2 IsPeriodic=0
    g295: BSplineCurve PolesCount=3 KnotsCount=2 Degree=2 IsPeriodic=0
    g296: BSplineCurve PolesCount=3 KnotsCount=2 Degree=2 IsPeriodic=0
    g297: BSplineCurve PolesCount=3 KnotsCount=2 Degree=2 IsPeriodic=0
    g298: BSplineCurve PolesCount=3 KnotsCount=2 Degree=2 IsPeriodic=0
    g299: BSplineCurve PolesCount=3 KnotsCount=2 Degree=2 IsPeriodic=0
    g300: BSplineCurve PolesCount=3 KnotsCount=2 Degree=2 IsPeriodic=0
    g301: BSplineCurve PolesCount=3 KnotsCount=2 Degree=2 IsPeriodic=0
    g302: BSplineCurve PolesCount=3 KnotsCount=2 Degree=2 IsPeriodic=0
    g303: BSplineCurve PolesCount=3 KnotsCount=2 Degree=2 IsPeriodic=0
    g304: BSplineCurve PolesCount=3 KnotsCount=2 Degree=2 IsPeriodic=0
    g305: BSplineCurve PolesCount=3 KnotsCount=2 Degree=2 IsPeriodic=0
    g306: BSplineCurve PolesCount=3 KnotsCount=2 Degree=2 IsPeriodic=0
    g307: BSplineCurve PolesCount=3 KnotsCount=2 Degree=2 IsPeriodic=0
    g308: BSplineCurve PolesCount=3 KnotsCount=2 Degree=2 IsPeriodic=0
    g309: BSplineCurve PolesCount=3 KnotsCount=2 Degree=2 IsPeriodic=0
    g310: BSplineCurve PolesCount=3 KnotsCount=2 Degree=2 IsPeriodic=0
    g311: BSplineCurve PolesCount=3 KnotsCount=2 Degree=2 IsPeriodic=0
    g312: BSplineCurve PolesCount=3 KnotsCount=2 Degree=2 IsPeriodic=0
    g313: BSplineCurve PolesCount=3 KnotsCount=2 Degree=2 IsPeriodic=0
    g314: BSplineCurve PolesCount=3 KnotsCount=2 Degree=2 IsPeriodic=0
    g315: BSplineCurve PolesCount=3 KnotsCount=2 Degree=2 IsPeriodic=0
    g316: BSplineCurve PolesCount=3 KnotsCount=2 Degree=2 IsPeriodic=0
    g317: BSplineCurve PolesCount=3 KnotsCount=2 Degree=2 IsPeriodic=0
    g318: BSplineCurve PolesCount=3 KnotsCount=2 Degree=2 IsPeriodic=0
    g319: BSplineCurve PolesCount=3 KnotsCount=2 Degree=2 IsPeriodic=0
    g320: BSplineCurve PolesCount=2 KnotsCount=2 Degree=1 IsPeriodic=0
    g321: BSplineCurve PolesCount=3 KnotsCount=2 Degree=2 IsPeriodic=0
    g322: BSplineCurve PolesCount=3 KnotsCount=2 Degree=2 IsPeriodic=0
    g323: BSplineCurve PolesCount=3 KnotsCount=2 Degree=2 IsPeriodic=0
    g324: BSplineCurve PolesCount=3 KnotsCount=2 Degree=2 IsPeriodic=0
    g325: BSplineCurve PolesCount=3 KnotsCount=2 Degree=2 IsPeriodic=0
    g326: BSplineCurve PolesCount=3 KnotsCount=2 Degree=2 IsPeriodic=0
    g327: BSplineCurve PolesCount=3 KnotsCount=2 Degree=2 IsPeriodic=0
    g328: BSplineCurve PolesCount=3 KnotsCount=2 Degree=2 IsPeriodic=0
    g329: BSplineCurve PolesCount=3 KnotsCount=2 Degree=2 IsPeriodic=0
    g330: BSplineCurve PolesCount=3 KnotsCount=2 Degree=2 IsPeriodic=0
    g331: BSplineCurve PolesCount=3 KnotsCount=2 Degree=2 IsPeriodic=0
    g332: BSplineCurve PolesCount=3 KnotsCount=2 Degree=2 IsPeriodic=0
    g333: BSplineCurve PolesCount=3 KnotsCount=2 Degree=2 IsPeriodic=0
    g334: BSplineCurve PolesCount=3 KnotsCount=2 Degree=2 IsPeriodic=0
    g335: BSplineCurve PolesCount=3 KnotsCount=2 Degree=2 IsPeriodic=0
    g336: BSplineCurve PolesCount=3 KnotsCount=2 Degree=2 IsPeriodic=0
    g337: BSplineCurve PolesCount=2 KnotsCount=2 Degree=1 IsPeriodic=0
    g338: BSplineCurve PolesCount=2 KnotsCount=2 Degree=1 IsPeriodic=0
    g339: BSplineCurve PolesCount=2 KnotsCount=2 Degree=1 IsPeriodic=0
    g340: BSplineCurve PolesCount=2 KnotsCount=2 Degree=1 IsPeriodic=0
    g341: BSplineCurve PolesCount=2 KnotsCount=2 Degree=1 IsPeriodic=0
    g342: BSplineCurve PolesCount=2 KnotsCount=2 Degree=1 IsPeriodic=0
    g343: BSplineCurve PolesCount=2 KnotsCount=2 Degree=1 IsPeriodic=0
    g344: BSplineCurve PolesCount=2 KnotsCount=2 Degree=1 IsPeriodic=0
    g345: BSplineCurve PolesCount=2 KnotsCount=2 Degree=1 IsPeriodic=0
    g346: BSplineCurve PolesCount=2 KnotsCount=2 Degree=1 IsPeriodic=0
    g347: BSplineCurve PolesCount=2 KnotsCount=2 Degree=1 IsPeriodic=0
    g348: BSplineCurve PolesCount=3 KnotsCount=2 Degree=2 IsPeriodic=0
    g349: BSplineCurve PolesCount=3 KnotsCount=2 Degree=2 IsPeriodic=0
    g350: BSplineCurve PolesCount=3 KnotsCount=2 Degree=2 IsPeriodic=0
    g351: BSplineCurve PolesCount=3 KnotsCount=2 Degree=2 IsPeriodic=0
    g352: BSplineCurve PolesCount=3 KnotsCount=2 Degree=2 IsPeriodic=0
    g353: BSplineCurve PolesCount=3 KnotsCount=2 Degree=2 IsPeriodic=0
    g354: BSplineCurve PolesCount=3 KnotsCount=2 Degree=2 IsPeriodic=0
    g355: BSplineCurve PolesCount=3 KnotsCount=2 Degree=2 IsPeriodic=0
    g356: BSplineCurve PolesCount=3 KnotsCount=2 Degree=2 IsPeriodic=0
    g357: BSplineCurve PolesCount=3 KnotsCount=2 Degree=2 IsPeriodic=0
    g358: BSplineCurve PolesCount=3 KnotsCount=2 Degree=2 IsPeriodic=0
    g359: BSplineCurve PolesCount=3 KnotsCount=2 Degree=2 IsPeriodic=0
    g360: BSplineCurve PolesCount=3 KnotsCount=2 Degree=2 IsPeriodic=0
    g361: BSplineCurve PolesCount=3 KnotsCount=2 Degree=2 IsPeriodic=0
    g362: BSplineCurve PolesCount=3 KnotsCount=2 Degree=2 IsPeriodic=0
    g363: BSplineCurve PolesCount=3 KnotsCount=2 Degree=2 IsPeriodic=0
    g364: BSplineCurve PolesCount=2 KnotsCount=2 Degree=1 IsPeriodic=0
    g365: BSplineCurve PolesCount=2 KnotsCount=2 Degree=1 IsPeriodic=0
    g366: BSplineCurve PolesCount=2 KnotsCount=2 Degree=1 IsPeriodic=0
    g367: BSplineCurve PolesCount=2 KnotsCount=2 Degree=1 IsPeriodic=0
    g368: BSplineCurve PolesCount=2 KnotsCount=2 Degree=1 IsPeriodic=0
    g369: BSplineCurve PolesCount=2 KnotsCount=2 Degree=1 IsPeriodic=0
    g370: BSplineCurve PolesCount=2 KnotsCount=2 Degree=1 IsPeriodic=0
    g371: BSplineCurve PolesCount=2 KnotsCount=2 Degree=1 IsPeriodic=0
    g372: BSplineCurve PolesCount=2 KnotsCount=2 Degree=1 IsPeriodic=0
    g373: BSplineCurve PolesCount=2 KnotsCount=2 Degree=1 IsPeriodic=0
    g374: BSplineCurve PolesCount=2 KnotsCount=2 Degree=1 IsPeriodic=0
    g375: BSplineCurve PolesCount=2 KnotsCount=2 Degree=1 IsPeriodic=0
    g376: BSplineCurve PolesCount=2 KnotsCount=2 Degree=1 IsPeriodic=0
    g377: BSplineCurve PolesCount=2 KnotsCount=2 Degree=1 IsPeriodic=0
    g378: BSplineCurve PolesCount=2 KnotsCount=2 Degree=1 IsPeriodic=0
    g379: BSplineCurve PolesCount=2 KnotsCount=2 Degree=1 IsPeriodic=0
    g380: BSplineCurve PolesCount=2 KnotsCount=2 Degree=1 IsPeriodic=0
    g381: BSplineCurve PolesCount=2 KnotsCount=2 Degree=1 IsPeriodic=0
    g382: BSplineCurve PolesCount=2 KnotsCount=2 Degree=1 IsPeriodic=0
    g383: BSplineCurve PolesCount=2 KnotsCount=2 Degree=1 IsPeriodic=0
    g384: BSplineCurve PolesCount=2 KnotsCount=2 Degree=1 IsPeriodic=0
    g385: BSplineCurve PolesCount=2 KnotsCount=2 Degree=1 IsPeriodic=0
    g386: BSplineCurve PolesCount=2 KnotsCount=2 Degree=1 IsPeriodic=0
    g387: BSplineCurve PolesCount=2 KnotsCount=2 Degree=1 IsPeriodic=0
    g388: BSplineCurve PolesCount=2 KnotsCount=2 Degree=1 IsPeriodic=0
    g389: BSplineCurve PolesCount=2 KnotsCount=2 Degree=1 IsPeriodic=0
    g390: BSplineCurve PolesCount=2 KnotsCount=2 Degree=1 IsPeriodic=0
    g391: BSplineCurve PolesCount=2 KnotsCount=2 Degree=1 IsPeriodic=0
    g392: BSplineCurve PolesCount=2 KnotsCount=2 Degree=1 IsPeriodic=0
    g393: BSplineCurve PolesCount=2 KnotsCount=2 Degree=1 IsPeriodic=0
    g394: BSplineCurve PolesCount=2 KnotsCount=2 Degree=1 IsPeriodic=0
    g395: BSplineCurve PolesCount=2 KnotsCount=2 Degree=1 IsPeriodic=0
    g396: BSplineCurve PolesCount=2 KnotsCount=2 Degree=1 IsPeriodic=0
    g397: BSplineCurve PolesCount=2 KnotsCount=2 Degree=1 IsPeriodic=0
    g398: BSplineCurve PolesCount=3 KnotsCount=2 Degree=2 IsPeriodic=0
    g399: BSplineCurve PolesCount=3 KnotsCount=2 Degree=2 IsPeriodic=0
    ... +790 more geometry lines
  constraints (1190):
    c: Coincident(g93,g94)
    c: Coincident(g92,g93)
    c: Coincident(g282,g284)
    c: Coincident(g273,g274)
    c: Coincident(g272,g273)
    c: Coincident(g280,g282)
    c: Coincident(g88,g89)
    c: Coincident(g96,g97)
    c: Coincident(g299,g300)
    c: Coincident(g284,g286)
    c: Coincident(g298,g299)
    c: Coincident(g96,g99)
    c: Coincident(g89,g90)
    c: Coincident(g280,g281)
    c: Coincident(g271,g272)
    c: Coincident(g298,g304)
    c: Coincident(g300,g301)
    c: Coincident(g286,g288)
    c: Coincident(g274,g275)
    c: Coincident(g281,g283)
    c: Coincident(g303,g304)
    c: Coincident(g301,g302)
    c: Coincident(g288,g290)
    c: Coincident(g302,g303)
    c: Coincident(g283,g285)
    c: Coincident(g285,g287)
    c: Coincident(g290,g292)
    c: Coincident(g292,g294)
    c: Coincident(g270,g271)
    c: Coincident(g306,g308)
    c: Coincident(g287,g289)
    c: Coincident(g249,g251)
    c: Coincident(g314,g316)
    c: Coincident(g305,g306)
    c: Coincident(g308,g310)
    c: Coincident(g294,g296)
    c: Coincident(g251,g253)
    c: Coincident(g312,g314)
    c: Coincident(g263,g264)
    c: Coincident(g322,g324)
    c: Coincident(g316,g318)
    c: Coincident(g264,g265)
    c: Coincident(g289,g291)
    c: Coincident(g305,g307)
    c: Coincident(g324,g326)
    c: Coincident(g247,g249)
    c: Coincident(g310,g311)
    c: Coincident(g296,g297)
    c: Coincident(g262,g263)
    c: Coincident(g276,g277)
    c: Coincident(g320,g322)
    c: Coincident(g318,g320)
    c: Coincident(g265,g266)
    c: Coincident(g309,g311)
    c: Coincident(g275,g276)
    c: Coincident(g307,g309)
    c: Coincident(g291,g293)
    c: Coincident(g270,g279)
    c: Coincident(g325,g327)
    c: Coincident(g323,g325)
    c: Coincident(g100,g101)
    c: Coincident(g84,g85)
    c: Coincident(g253,g255)
    c: Coincident(g295,g297)
    c: Coincident(g277,g278)
    c: Coincident(g262,g269)
    c: Coincident(g312,g313)
    c: Coincident(g326,g327)
    c: Coincident(g247,g248)
    c: Coincident(g293,g295)
    c: Coincident(g329,g330)
    c: Coincident(g330,g331)
    c: Coincident(g278,g279)
    c: Coincident(g254,g256)
    c: Coincident(g266,g267)
    c: Coincident(g85,g86)
    c: Coincident(g100,g103)
    c: Coincident(g328,g329)
    c: Coincident(g321,g323)
    c: Coincident(g268,g269)
    c: Coincident(g267,g268)
    c: Coincident(g331,g332)
    c: Coincident(g94,g95)
    c: Coincident(g92,g95)
    c: Coincident(g252,g254)
    c: Coincident(g328,g336)
    c: Coincident(g248,g250)
    c: Coincident(g250,g252)
    c: Coincident(g332,g333)
    c: Coincident(g256,g258)
    c: Coincident(g319,g321)
    c: Coincident(g335,g336)
    c: Coincident(g255,g257)
    c: Coincident(g313,g315)
    c: Coincident(g88,g91)
    c: Coincident(g97,g98)
    c: Coincident(g260,g261)
    c: Coincident(g98,g99)
    c: Coincident(g90,g91)
    c: Coincident(g333,g334)
    c: Coincident(g259,g261)
    c: Coincident(g334,g335)
    c: Coincident(g258,g260)
    c: Coincident(g317,g319)
    c: Coincident(g348,g350)
    c: Coincident(g350,g352)
    c: Coincident(g315,g317)
    c: Coincident(g257,g259)
    c: Coincident(g357,g358)
    c: Coincident(g356,g357)
    c: Coincident(g228,g229)
    c: Coincident(g227,g228)
    c: Coincident(g346,g347)
    c: Coincident(g229,g230)
    c: Coincident(g352,g354)
    c: Coincident(g358,g359)
    c: Coincident(g231,g232)
    c: Coincident(g348,g349)
    c: Coincident(g230,g231)
    c: Coincident(g345,g346)
    c: Coincident(g356,g363)
    c: Coincident(g226,g227)
    c: Coincident(g232,g233)
    c: Coincident(g344,g345)
    c: Coincident(g238,g239)
    c: Coincident(g338,g339)
    c: Coincident(g237,g238)
    c: Coincident(g337,g347)
    c: Coincident(g359,g360)
    c: Coincident(g233,g234)
    c: Coincident(g236,g237)
    c: Coincident(g101,g102)
    c: Coincident(g84,g87)
    c: Coincident(g354,g355)
    c: Coincident(g243,g244)
    c: Coincident(g337,g338)
    c: Coincident(g362,g363)
    c: Coincident(g226,g246)
    c: Coincident(g349,g351)
    c: Coincident(g235,g236)
    c: Coincident(g234,g235)
    c: Coincident(g102,g103)
    c: Coincident(g86,g87)
    c: Coincident(g244,g245)
    c: Coincident(g80,g81)
    c: Coincident(g104,g105)
    c: Coincident(g245,g246)
    c: Coincident(g360,g361)
    c: Coincident(g361,g362)
    c: Coincident(g351,g353)
    c: Coincident(g242,g243)
    c: Coincident(g353,g355)
    c: Coincident(g239,g240)
    c: Coincident(g81,g82)
    c: Coincident(g104,g107)
    c: Coincident(g241,g242)
    c: Coincident(g340,g341)
    c: Coincident(g339,g340)
    c: Coincident(g240,g241)
    c: Coincident(g343,g344)
    c: Coincident(g341,g342)
    c: Coincident(g342,g343)
    c: Coincident(g384,g385)
    c: Coincident(g383,g384)
    c: Coincident(g382,g383)
    c: Coincident(g376,g377)
    c: Coincident(g214,g216)
    c: Coincident(g375,g385)
    c: Coincident(g373,g374)
    c: Coincident(g216,g218)
    c: Coincident(g80,g83)
    c: Coincident(g105,g106)
    c: Coincident(g375,g376)
    c: Coincident(g210,g212)
    c: Coincident(g220,g221)
    c: Coincident(g372,g373)
    c: Coincident(g221,g222)
    c: Coincident(g208,g210)
    c: Coincident(g222,g223)
    c: Coincident(g106,g107)
    c: Coincident(g82,g83)
    c: Coincident(g212,g214)
    c: Coincident(g371,g372)
    c: Coincident(g208,g209)
    c: Coincident(g219,g220)
    c: Coincident(g365,g366)
    c: Coincident(g213,g215)
    c: Coincident(g209,g211)
    c: Coincident(g364,g374)
    c: Coincident(g377,g378)
    c: Coincident(g211,g213)
    c: Coincident(g364,g365)
    c: Coincident(g381,g382)
    c: Coincident(g378,g379)
    c: Coincident(g380,g381)
    c: Coincident(g379,g380)
    c: Coincident(g223,g224)
    c: Coincident(g224,g225)
    c: Coincident(g219,g225)
    c: Coincident(g217,g218)
    c: Coincident(g108,g109)
    c: Coincident(g76,g77)
    c: Coincident(g215,g217)
    c: Coincident(g366,g367)
    c: Coincident(g370,g371)
    c: Coincident(g367,g368)
    c: Coincident(g369,g370)
    c: Coincident(g368,g369)
    c: Coincident(g108,g111)
    c: Coincident(g77,g78)
    c: Coincident(g419,g420)
    c: Coincident(g418,g419)
    c: Coincident(g109,g110)
    c: Coincident(g76,g79)
    c: Coincident(g78,g79)
    c: Coincident(g110,g111)
    c: Coincident(g181,g182)
    c: Coincident(g414,g415)
    c: Coincident(g413,g414)
    c: Coincident(g415,g416)
    c: Coincident(g182,g183)
    c: Coincident(g417,g418)
    c: Coincident(g412,g413)
    c: Coincident(g416,g417)
    c: Coincident(g397,g420)
    c: Coincident(g401,g402)
    c: Coincident(g402,g403)
    c: Coincident(g400,g401)
    c: Coincident(g180,g181)
    c: Coincident(g397,g398)
    c: Coincident(g183,g184)
    c: Coincident(g403,g404)
    c: Coincident(g399,g400)
    c: Coincident(g398,g399)
    c: Coincident(g395,g396)
    c: Coincident(g184,g185)
    c: Coincident(g411,g412)
    c: Coincident(g394,g395)
    c: Coincident(g404,g405)
    c: Coincident(g189,g190)
    c: Coincident(g185,g186)
    c: Coincident(g198,g199)
    c: Coincident(g179,g180)
    c: Coincident(g188,g189)
    c: Coincident(g405,g406)
    c: Coincident(g190,g191)
    c: Coincident(g407,g408)
    c: Coincident(g393,g394)
    c: Coincident(g197,g198)
    c: Coincident(g191,g192)
    c: Coincident(g410,g411)
    c: Coincident(g406,g407)
    c: Coincident(g186,g187)
    c: Coincident(g187,g188)
    c: Coincident(g205,g206)
    c: Coincident(g204,g205)
    c: Coincident(g387,g388)
    c: Coincident(g408,g409)
    c: Coincident(g199,g200)
    c: Coincident(g179,g207)
    c: Coincident(g196,g197)
    c: Coincident(g409,g410)
    c: Coincident(g192,g193)
    c: Coincident(g206,g207)
    c: Coincident(g386,g396)
    c: Coincident(g195,g196)
    c: Coincident(g203,g204)
    c: Coincident(g386,g387)
    c: Coincident(g193,g194)
    c: Coincident(g200,g201)
    c: Coincident(g194,g195)
    c: Coincident(g202,g203)
    c: Coincident(g201,g202)
    c: Coincident(g392,g393)
    c: Coincident(g388,g389)
    c: Coincident(g391,g392)
    c: Coincident(g389,g390)
    c: Coincident(g112,g113)
    c: Coincident(g72,g73)
    c: Coincident(g390,g391)
    c: Coincident(g73,g74)
    c: Coincident(g112,g115)
    c: Coincident(g72,g75)
    c: Coincident(g113,g114)
    c: Coincident(g432,g433)
    c: Coincident(g432,g460)
    c: Coincident(g74,g75)
    c: Coincident(g114,g115)
    c: Coincident(g438,g439)
    c: Coincident(g439,g440)
    c: Coincident(g459,g460)
    c: Coincident(g433,g434)
    c: Coincident(g437,g438)
    c: Coincident(g456,g457)
    c: Coincident(g440,g441)
    c: Coincident(g155,g178)
    c: Coincident(g455,g456)
    c: Coincident(g155,g156)
    c: Coincident(g458,g459)
    c: Coincident(g457,g458)
    c: Coincident(g445,g446)
    c: Coincident(g446,g447)
    c: Coincident(g434,g435)
    c: Coincident(g175,g176)
    c: Coincident(g454,g455)
    c: Coincident(g441,g442)
    c: Coincident(g156,g157)
    c: Coincident(g447,g448)
    c: Coincident(g444,g445)
    c: Coincident(g442,g443)
    c: Coincident(g436,g437)
    c: Coincident(g174,g175)
    c: Coincident(g443,g444)
    c: Coincident(g157,g158)
    c: Coincident(g430,g431)
    c: Coincident(g166,g167)
    c: Coincident(g435,g436)
    c: Coincident(g448,g449)
    c: Coincident(g429,g430)
    c: Coincident(g453,g454)
    c: Coincident(g173,g174)
    c: Coincident(g450,g451)
    c: Coincident(g449,g450)
    c: Coincident(g165,g166)
    c: Coincident(g158,g159)
    c: Coincident(g167,g168)
    c: Coincident(g164,g165)
    c: Coincident(g451,g452)
    c: Coincident(g452,g453)
    c: Coincident(g177,g178)
    c: Coincident(g159,g160)
    c: Coincident(g428,g429)
    c: Coincident(g176,g177)
    c: Coincident(g172,g173)
    c: Coincident(g163,g164)
    c: Coincident(g160,g161)
    c: Coincident(g422,g423)
    c: Coincident(g168,g169)
    c: Coincident(g161,g162)
    c: Coincident(g162,g163)
    c: Coincident(g171,g172)
    c: Coincident(g421,g431)
    c: Coincident(g170,g171)
    c: Coincident(g169,g170)
    c: Coincident(g421,g422)
    c: Coincident(g427,g428)
    c: Coincident(g423,g424)
    c: Coincident(g426,g427)
    c: Coincident(g424,g425)
    c: Coincident(g425,g426)
    c: Coincident(g68,g69)
    c: Coincident(g116,g117)
    c: Coincident(g116,g119)
    c: Coincident(g69,g70)
    c: Coincident(g68,g71)
    c: Coincident(g117,g118)
    c: Coincident(g118,g119)
    c: Coincident(g70,g71)
    c: Coincident(g473,g475)
    c: Coincident(g475,g477)
    c: Coincident(g472,g474)
    c: Coincident(g472,g473)
    c: Coincident(g477,g479)
    c: Coincident(g474,g476)
    c: Coincident(g476,g478)
    c: Coincident(g483,g484)
    c: Coincident(g479,g481)
    c: Coincident(g144,g154)
    c: Coincident(g144,g145)
    c: Coincident(g483,g489)
    c: Coincident(g488,g489)
    c: Coincident(g487,g488)
    c: Coincident(g481,g482)
    c: Coincident(g486,g487)
    c: Coincident(g485,g486)
    c: Coincident(g484,g485)
    c: Coincident(g147,g148)
    c: Coincident(g148,g149)
    c: Coincident(g145,g146)
    c: Coincident(g478,g480)
    c: Coincident(g480,g482)
    c: Coincident(g470,g471)
    c: Coincident(g469,g470)
    c: Coincident(g151,g152)
    c: Coincident(g146,g147)
    c: Coincident(g149,g150)
    c: Coincident(g153,g154)
    c: Coincident(g468,g469)
    c: Coincident(g152,g153)
    c: Coincident(g150,g151)
    c: Coincident(g462,g463)
    c: Coincident(g467,g468)
    c: Coincident(g461,g471)
    c: Coincident(g463,g464)
    c: Coincident(g461,g462)
    c: Coincident(g466,g467)
    c: Coincident(g464,g465)
    c: Coincident(g465,g466)
    c: Coincident(g64,g65)
    c: Coincident(g120,g121)
    c: Coincident(g121,g122)
    c: Coincident(g64,g67)
    c: Coincident(g120,g123)
    c: Coincident(g65,g66)
    c: Coincident(g122,g123)
    c: Coincident(g66,g67)
    c: Coincident(g501,g521)
    c: Coincident(g501,g502)
    c: Coincident(g520,g521)
    c: Coincident(g516,g517)
    c: Coincident(g515,g516)
    c: Coincident(g508,g509)
    c: Coincident(g507,g508)
    c: Coincident(g509,g510)
    c: Coincident(g502,g503)
    c: Coincident(g506,g507)
    c: Coincident(g519,g520)
    c: Coincident(g510,g511)
    c: Coincident(g134,g135)
    c: Coincident(g511,g512)
    c: Coincident(g132,g134)
    c: Coincident(g133,g135)
    c: Coincident(g139,g140)
    c: Coincident(g512,g513)
    c: Coincident(g505,g506)
    c: Coincident(g503,g504)
    c: Coincident(g518,g519)
    c: Coincident(g517,g518)
    c: Coincident(g138,g139)
    c: Coincident(g140,g141)
    c: Coincident(g513,g514)
    c: Coincident(g504,g505)
    c: Coincident(g514,g515)
    c: Coincident(g130,g132)
    c: Coincident(g137,g138)
    c: Coincident(g499,g500)
    c: Coincident(g498,g499)
    c: Coincident(g141,g142)
    c: Coincident(g131,g133)
    c: Coincident(g136,g137)
    c: Coincident(g142,g143)
    c: Coincident(g136,g143)
    c: Coincident(g128,g130)
    c: Coincident(g497,g498)
    c: Coincident(g129,g131)
    c: Coincident(g128,g129)
    c: Coincident(g496,g497)
    c: Coincident(g491,g492)
    c: Coincident(g492,g493)
    c: Coincident(g495,g496)
    c: Coincident(g490,g500)
    c: Coincident(g490,g491)
    c: Coincident(g493,g494)
    c: Coincident(g494,g495)
    c: Coincident(g124,g125)
    c: Coincident(g125,g126)
    c: Coincident(g60,g61)
    c: Coincident(g61,g62)
    c: Coincident(g60,g63)
    c: Coincident(g62,g63)
    c: Coincident(g124,g127)
    c: Coincident(g126,g127)
    c: Coincident(g1169,g1170)
    c: Coincident(g545,g547)
    c: Coincident(g1153,g1154)
    c: Coincident(g533,g534)
    c: Coincident(g1170,g1171)
    c: Coincident(g534,g536)
    c: Coincident(g1168,g1169)
    c: Coincident(g546,g547)
    c: Coincident(g533,g535)
    c: Coincident(g1152,g1153)
    c: Coincident(g548,g555)
    c: Coincident(g1154,g1155)
    c: Coincident(g1167,g1168)
    c: Coincident(g554,g555)
    c: Coincident(g548,g549)
    c: Coincident(g1161,g1162)
    c: Coincident(g1160,g1161)
    c: Coincident(g543,g545)
    c: Coincident(g544,g546)
    c: Coincident(g1171,g1172)
    c: Coincident(g536,g538)
    c: Coincident(g1166,g1167)
    c: Coincident(g1162,g1163)
    c: Coincident(g1159,g1160)
    c: Coincident(g553,g554)
    c: Coincident(g549,g550)
    c: Coincident(g535,g537)
    c: Coincident(g1155,g1156)
    c: Coincident(g1151,g1152)
    c: Coincident(g538,g540)
    c: Coincident(g1165,g1166)
    c: Coincident(g1175,g1176)
    c: Coincident(g1176,g1177)
    c: Coincident(g542,g544)
    c: Coincident(g1163,g1164)
    c: Coincident(g552,g553)
    c: Coincident(g1158,g1159)
    c: Coincident(g1164,g1165)
    c: Coincident(g550,g551)
    c: Coincident(g1172,g1173)
    c: Coincident(g1156,g1157)
    c: Coincident(g541,g543)
    c: Coincident(g540,g542)
    c: Coincident(g551,g552)
    c: Coincident(g1157,g1158)
    c: Coincident(g1174,g1175)
    c: Coincident(g537,g539)
    c: Coincident(g1177,g1178)
    c: Coincident(g1173,g1174)
    c: Coincident(g1150,g1151)
    c: Coincident(g539,g541)
    c: Coincident(g1150,g1178)
    c: Coincident(g1183,g1184)
    c: Coincident(g530,g531)
    c: Coincident(g1182,g1183)
    c: Coincident(g531,g532)
    c: Coincident(g1179,g1180)
    c: Coincident(g1179,g1189)
    c: Coincident(g528,g529)
    c: Coincident(g1184,g1185)
    c: Coincident(g1181,g1182)
    c: Coincident(g529,g530)
    c: Coincident(g527,g528)
    c: Coincident(g1180,g1181)
    c: Coincident(g524,g525)
    c: Coincident(g1185,g1186)
    c: Coincident(g523,g524)
    c: Coincident(g1186,g1187)
    c: Coincident(g526,g527)
    c: Coincident(g525,g526)
    c: Coincident(g522,g523)
    c: Coincident(g522,g532)
    c: Coincident(g1187,g1188)
    c: Coincident(g1188,g1189)
    c: Coincident(g56,g57)
    c: Coincident(g0,g1)
    c: Coincident(g0,g3)
    c: Coincident(g57,g58)
    c: Coincident(g1,g2)
    c: Coincident(g56,g59)
    c: Coincident(g2,g3)
    c: Coincident(g58,g59)
    c: Coincident(g575,g576)
    c: Coincident(g567,g576)
    c: Coincident(g1124,g1125)
    c: Coincident(g1125,g1126)
    c: Coincident(g572,g573)
    c: Coincident(g1123,g1124)
    c: Coincident(g1108,g1109)
    c: Coincident(g1122,g1123)
    c: Coincident(g1126,g1127)
    c: Coincident(g1109,g1110)
    c: Coincident(g1121,g1122)
    c: Coincident(g1116,g1117)
    c: Coincident(g567,g568)
    c: Coincident(g1107,g1108)
    c: Coincident(g1115,g1116)
    c: Coincident(g1117,g1118)
    c: Coincident(g1114,g1115)
    c: Coincident(g1120,g1121)
    c: Coincident(g568,g569)
    c: Coincident(g1118,g1119)
    c: Coincident(g571,g572)
    c: Coincident(g1127,g1128)
    c: Coincident(g1130,g1131)
    c: Coincident(g1131,g1132)
    c: Coincident(g1119,g1120)
    c: Coincident(g1110,g1111)
    c: Coincident(g1106,g1107)
    c: Coincident(g569,g570)
    c: Coincident(g1113,g1114)
    c: Coincident(g574,g575)
    c: Coincident(g573,g574)
    c: Coincident(g1129,g1130)
    c: Coincident(g1128,g1129)
    c: Coincident(g1111,g1112)
    c: Coincident(g1112,g1113)
    c: Coincident(g570,g571)
    c: Coincident(g1132,g1133)
    c: Coincident(g1105,g1106)
    c: Coincident(g1105,g1133)
    c: Coincident(g1139,g1141)
    c: Coincident(g1140,g1141)
    c: Coincident(g1146,g1147)
    c: Coincident(g562,g563)
    c: Coincident(g1145,g1146)
    c: Coincident(g564,g565)
    c: Coincident(g565,g566)
    c: Coincident(g1137,g1139)
    c: Coincident(g1138,g1140)
    c: Coincident(g561,g562)
    c: Coincident(g1147,g1148)
    c: Coincident(g558,g559)
    c: Coincident(g1144,g1145)
    c: Coincident(g563,g564)
    c: Coincident(g1148,g1149)
    c: Coincident(g1143,g1144)
    c: Coincident(g1135,g1137)
    c: Coincident(g1136,g1138)
    c: Coincident(g557,g558)
    c: Coincident(g560,g561)
    c: Coincident(g559,g560)
    c: Coincident(g1142,g1149)
    c: Coincident(g1142,g1143)
    c: Coincident(g1134,g1135)
    c: Coincident(g1134,g1136)
    c: Coincident(g556,g557)
    c: Coincident(g556,g566)
    c: Coincident(g4,g5)
    c: Coincident(g52,g53)
    c: Coincident(g5,g6)
    c: Coincident(g52,g55)
    c: Coincident(g53,g54)
    c: Coincident(g4,g7)
    c: Coincident(g54,g55)
    c: Coincident(g6,g7)
    c: Coincident(g599,g601)
    c: Coincident(g1068,g1069)
    c: Coincident(g1067,g1068)
    c: Coincident(g597,g599)
    c: Coincident(g1065,g1066)
    c: Coincident(g595,g597)
    c: Coincident(g1066,g1067)
    c: Coincident(g613,g615)
    c: Coincident(g601,g603)
    c: Coincident(g1069,g1070)
    c: Coincident(g589,g591)
    c: Coincident(g588,g589)
    c: Coincident(g615,g617)
    c: Coincident(g1064,g1065)
    c: Coincident(g613,g614)
    c: Coincident(g593,g595)
    c: Coincident(g591,g593)
    c: Coincident(g611,g612)
    c: Coincident(g1056,g1057)
    c: Coincident(g1057,g1058)
    c: Coincident(g606,g612)
    c: Coincident(g1056,g1079)
    c: Coincident(g617,g619)
    c: Coincident(g1063,g1064)
    c: Coincident(g1058,g1059)
    c: Coincident(g614,g616)
    c: Coincident(g588,g590)
    c: Coincident(g603,g605)
    c: Coincident(g1070,g1071)
    c: Coincident(g1059,g1060)
    c: Coincident(g610,g611)
    c: Coincident(g1076,g1077)
    c: Coincident(g1075,g1076)
    c: Coincident(g606,g607)
    c: Coincident(g618,g619)
    c: Coincident(g1062,g1063)
    c: Coincident(g1060,g1061)
    c: Coincident(g616,g618)
    c: Coincident(g1061,g1062)
    c: Coincident(g1074,g1075)
    c: Coincident(g600,g602)
    c: Coincident(g598,g600)
    c: Coincident(g604,g605)
    c: Coincident(g1071,g1072)
    c: Coincident(g609,g610)
    c: Coincident(g1073,g1074)
    c: Coincident(g602,g604)
    c: Coincident(g607,g608)
    c: Coincident(g1072,g1073)
    c: Coincident(g590,g592)
    c: Coincident(g596,g598)
    c: Coincident(g608,g609)
    c: Coincident(g1085,g1087)
    c: Coincident(g1087,g1089)
    c: Coincident(g583,g584)
    c: Coincident(g594,g596)
    c: Coincident(g1101,g1102)
    c: Coincident(g592,g594)
    c: Coincident(g1100,g1101)
    c: Coincident(g1083,g1085)
    c: Coincident(g1077,g1078)
    c: Coincident(g582,g583)
    c: Coincident(g1102,g1103)
    c: Coincident(g1089,g1091)
    c: Coincident(g1078,g1079)
    c: Coincident(g579,g580)
    c: Coincident(g1099,g1100)
    c: Coincident(g1086,g1088)
    c: Coincident(g585,g586)
    c: Coincident(g586,g587)
    c: Coincident(g1088,g1090)
    c: Coincident(g1103,g1104)
    c: Coincident(g1098,g1099)
    c: Coincident(g1084,g1086)
    c: Coincident(g1081,g1083)
    c: Coincident(g1091,g1093)
    c: Coincident(g581,g582)
    c: Coincident(g1097,g1098)
    c: Coincident(g584,g585)
    c: Coincident(g1096,g1104)
    c: Coincident(g580,g581)
    c: Coincident(g1096,g1097)
    c: Coincident(g1093,g1095)
    c: Coincident(g1090,g1092)
    c: Coincident(g1094,g1095)
    c: Coincident(g578,g579)
    c: Coincident(g1082,g1084)
    c: Coincident(g1092,g1094)
    c: Coincident(g1080,g1081)
    c: Coincident(g48,g49)
    c: Coincident(g8,g9)
    c: Coincident(g1080,g1082)
    c: Coincident(g577,g578)
    c: Coincident(g577,g587)
    c: Coincident(g9,g10)
    c: Coincident(g48,g51)
    c: Coincident(g8,g11)
    c: Coincident(g49,g50)
    c: Coincident(g1012,g1013)
    c: Coincident(g632,g634)
    c: Coincident(g50,g51)
    c: Coincident(g10,g11)
    c: Coincident(g1011,g1012)
    c: Coincident(g1009,g1010)
    c: Coincident(g1013,g1014)
    c: Coincident(g634,g636)
    c: Coincident(g654,g655)
    c: Coincident(g1010,g1011)
    c: Coincident(g631,g632)
    c: Coincident(g1008,g1009)
    c: Coincident(g653,g654)
    c: Coincident(g647,g655)
    c: Coincident(g647,g648)
    c: Coincident(g645,g646)
    c: Coincident(g1007,g1008)
    c: Coincident(g652,g653)
    c: Coincident(g1014,g1015)
    c: Coincident(g636,g638)
    c: Coincident(g648,g649)
    c: Coincident(g1001,g1002)
    c: Coincident(g644,g646)
    c: Coincident(g1002,g1003)
    c: Coincident(g1006,g1007)
    c: Coincident(g1000,g1001)
    c: Coincident(g1003,g1004)
    c: Coincident(g1005,g1006)
    c: Coincident(g1004,g1005)
    c: Coincident(g649,g650)
    c: Coincident(g651,g652)
    c: Coincident(g631,g633)
    c: Coincident(g1000,g1023)
    c: Coincident(g643,g645)
    c: Coincident(g1019,g1020)
    c: Coincident(g1015,g1016)
    c: Coincident(g1020,g1021)
    c: Coincident(g1018,g1019)
    c: Coincident(g650,g651)
    c: Coincident(g642,g644)
    c: Coincident(g1016,g1017)
    c: Coincident(g638,g640)
    c: Coincident(g1017,g1018)
    c: Coincident(g1039,g1041)
    c: Coincident(g1040,g1041)
    c: Coincident(g626,g627)
    c: Coincident(g640,g642)
    c: Coincident(g1053,g1055)
    c: Coincident(g641,g643)
    c: Coincident(g1037,g1039)
    c: Coincident(g1054,g1055)
    c: Coincident(g625,g626)
    c: Coincident(g639,g641)
    c: Coincident(g633,g635)
    c: Coincident(g1038,g1040)
    c: Coincident(g1051,g1053)
    c: Coincident(g622,g623)
    c: Coincident(g637,g639)
    c: Coincident(g1032,g1034)
    c: Coincident(g1052,g1054)
    c: Coincident(g635,g637)
    c: Coincident(g1036,g1038)
    c: Coincident(g1034,g1036)
    c: Coincident(g1030,g1032)
    c: Coincident(g1021,g1022)
    c: Coincident(g1035,g1037)
    c: Coincident(g1045,g1046)
    c: Coincident(g1022,g1023)
    c: Coincident(g1050,g1052)
    c: Coincident(g1044,g1045)
    c: Coincident(g1049,g1051)
    c: Coincident(g624,g625)
    c: Coincident(g628,g629)
    c: Coincident(g1046,g1047)
    c: Coincident(g1049,g1050)
    c: Coincident(g629,g630)
    c: Coincident(g623,g624)
    c: Coincident(g1033,g1035)
    c: Coincident(g1028,g1030)
    c: Coincident(g1029,g1031)
    c: Coincident(g1027,g1029)
    c: Coincident(g1031,g1033)
    c: Coincident(g1047,g1048)
    c: Coincident(g12,g13)
    c: Coincident(g44,g45)
    c: Coincident(g627,g628)
    c: Coincident(g1025,g1027)
    c: Coincident(g1043,g1044)
    c: Coincident(g621,g622)
    c: Coincident(g1042,g1048)
    c: Coincident(g1026,g1028)
    c: Coincident(g1042,g1043)
    c: Coincident(g44,g47)
    c: Coincident(g13,g14)
    c: Coincident(g1024,g1025)
    c: Coincident(g1024,g1026)
    c: Coincident(g620,g621)
    c: Coincident(g620,g630)
    c: Coincident(g978,g979)
    c: Coincident(g681,g683)
    c: Coincident(g45,g46)
    c: Coincident(g12,g15)
    c: Coincident(g977,g978)
    c: Coincident(g683,g685)
    c: Coincident(g979,g980)
    c: Coincident(g975,g976)
    c: Coincident(g694,g695)
    c: Coincident(g693,g694)
    c: Coincident(g974,g975)
    c: Coincident(g976,g977)
    c: Coincident(g680,g681)
    c: Coincident(g14,g15)
    c: Coincident(g46,g47)
    c: Coincident(g973,g974)
    c: Coincident(g980,g981)
    c: Coincident(g688,g695)
    c: Coincident(g692,g693)
    c: Coincident(g685,g687)
    c: Coincident(g997,g998)
    c: Coincident(g972,g973)
    c: Coincident(g971,g972)
    c: Coincident(g996,g997)
    c: Coincident(g981,g982)
    c: Coincident(g670,g671)
    c: Coincident(g970,g971)
    c: Coincident(g969,g970)
    c: Coincident(g968,g969)
    c: Coincident(g967,g968)
    c: Coincident(g982,g983)
    c: Coincident(g966,g967)
    c: Coincident(g669,g670)
    c: Coincident(g983,g984)
    c: Coincident(g671,g672)
    c: Coincident(g680,g682)
    c: Coincident(g688,g689)
    c: Coincident(g984,g985)
    c: Coincident(g691,g692)
    c: Coincident(g663,g664)
    c: Coincident(g985,g986)
    c: Coincident(g966,g989)
    c: Coincident(g986,g987)
    c: Coincident(g664,g665)
    c: Coincident(g662,g663)
    c: Coincident(g686,g687)
    c: Coincident(g672,g673)
    c: Coincident(g668,g669)
    c: Coincident(g665,g666)
    c: Coincident(g661,g662)
    c: Coincident(g689,g690)
    c: Coincident(g998,g999)
    c: Coincident(g995,g996)
    c: Coincident(g690,g691)
    c: Coincident(g673,g674)
    c: Coincident(g682,g684)
    c: Coincident(g990,g999)
    c: Coincident(g660,g661)
    c: Coincident(g40,g41)
    c: Coincident(g16,g17)
    c: Coincident(g666,g667)
    c: Coincident(g684,g686)
    c: Coincident(g987,g988)
    c: Coincident(g667,g668)
    c: Coincident(g994,g995)
    c: Coincident(g990,g991)
    c: Coincident(g659,g660)
    c: Coincident(g988,g989)
    c: Coincident(g677,g678)
    c: Coincident(g17,g18)
    c: Coincident(g40,g43)
    c: Coincident(g674,g675)
    c: Coincident(g678,g679)
    c: Coincident(g991,g992)
    c: Coincident(g658,g659)
    c: Coincident(g993,g994)
    c: Coincident(g675,g676)
    c: Coincident(g657,g658)
    c: Coincident(g992,g993)
    c: Coincident(g676,g677)
    c: Coincident(g656,g657)
    c: Coincident(g656,g679)
    c: Coincident(g931,g932)
    c: Coincident(g726,g727)
    c: Coincident(g932,g933)
    c: Coincident(g725,g726)
    c: Coincident(g928,g929)
    c: Coincident(g930,g931)
    c: Coincident(g927,g928)
    c: Coincident(g722,g723)
    c: Coincident(g929,g930)
    c: Coincident(g933,g934)
    c: Coincident(g926,g927)
    c: Coincident(g724,g725)
    c: Coincident(g41,g42)
    c: Coincident(g16,g19)
    c: Coincident(g925,g926)
    c: Coincident(g710,g711)
    c: Coincident(g709,g710)
    c: Coincident(g723,g724)
    c: Coincident(g934,g935)
    c: Coincident(g951,g953)
    c: Coincident(g953,g955)
    c: Coincident(g924,g925)
    c: Coincident(g703,g704)
    c: Coincident(g923,g924)
    c: Coincident(g42,g43)
    c: Coincident(g18,g19)
    c: Coincident(g704,g705)
    c: Coincident(g711,g712)
    c: Coincident(g935,g936)
    c: Coincident(g954,g956)
    c: Coincident(g922,g923)
    c: Coincident(g952,g954)
    c: Coincident(g921,g922)
    c: Coincident(g702,g703)
    c: Coincident(g936,g937)
    c: Coincident(g36,g37)
    c: Coincident(g20,g21)
    c: Coincident(g708,g709)
    c: Coincident(g920,g921)
    c: Coincident(g705,g706)
    c: Coincident(g712,g713)
    c: Coincident(g937,g938)
    c: Coincident(g728,g729)
    c: Coincident(g701,g702)
    c: Coincident(g938,g939)
    c: Coincident(g36,g39)
    c: Coincident(g21,g22)
    c: Coincident(g919,g920)
    c: Coincident(g956,g957)
    c: Coincident(g948,g950)
    c: Coincident(g949,g951)
    c: Coincident(g955,g957)
    c: Coincident(g939,g940)
    c: Coincident(g706,g707)
    c: Coincident(g946,g948)
    c: Coincident(g950,g952)
    c: Coincident(g713,g714)
    c: Coincident(g729,g730)
    c: Coincident(g919,g942)
    c: Coincident(g727,g728)
    c: Coincident(g700,g701)
    c: Coincident(g707,g708)
    c: Coincident(g962,g963)
    c: Coincident(g963,g964)
    c: Coincident(g721,g722)
    c: Coincident(g961,g962)
    c: Coincident(g699,g700)
    c: Coincident(g944,g946)
    c: Coincident(g964,g965)
    c: Coincident(g720,g721)
    c: Coincident(g940,g941)
    c: Coincident(g714,g715)
    c: Coincident(g717,g718)
    c: Coincident(g698,g699)
    c: Coincident(g720,g730)
    c: Coincident(g941,g942)
    c: Coincident(g947,g949)
    c: Coincident(g960,g961)
    c: Coincident(g958,g965)
    c: Coincident(g718,g719)
    c: Coincident(g715,g716)
    c: Coincident(g943,g944)
    c: Coincident(g768,g769)
    c: Coincident(g769,g770)
    c: Coincident(g887,g888)
    c: Coincident(g886,g887)
    c: Coincident(g697,g698)
    c: Coincident(g959,g960)
    c: Coincident(g958,g959)
    c: Coincident(g763,g764)
    c: Coincident(g716,g717)
    c: Coincident(g882,g883)
    c: Coincident(g762,g763)
    c: Coincident(g883,g884)
    c: Coincident(g945,g947)
    c: Coincident(g767,g768)
    c: Coincident(g888,g889)
    c: Coincident(g885,g886)
    c: Coincident(g943,g945)
    c: Coincident(g911,g912)
    c: Coincident(g770,g771)
    c: Coincident(g764,g765)
    c: Coincident(g696,g697)
    c: Coincident(g881,g882)
    c: Coincident(g884,g885)
    c: Coincident(g761,g762)
    c: Coincident(g24,g25)
    c: Coincident(g32,g33)
    c: Coincident(g744,g745)
    c: Coincident(g745,g746)
    c: Coincident(g696,g719)
    c: Coincident(g25,g26)
    c: Coincident(g32,g35)
    c: Coincident(g771,g772)
    c: Coincident(g914,g915)
    c: Coincident(g765,g766)
    c: Coincident(g880,g881)
    c: Coincident(g760,g761)
    c: Coincident(g912,g913)
    c: Coincident(g739,g740)
    c: Coincident(g738,g739)
    c: Coincident(g766,g767)
    c: Coincident(g889,g890)
    c: Coincident(g743,g744)
    c: Coincident(g746,g747)
    c: Coincident(g879,g880)
    c: Coincident(g740,g741)
    c: Coincident(g772,g773)
    c: Coincident(g759,g760)
    c: Coincident(g913,g914)
    c: Coincident(g737,g738)
    c: Coincident(g890,g891)
    c: Coincident(g878,g879)
    c: Coincident(g747,g748)
    c: Coincident(g28,g29)
    c: Coincident(g29,g30)
    c: Coincident(g877,g878)
    c: Coincident(g891,g892)
    c: Coincident(g758,g759)
    c: Coincident(g741,g742)
    c: Coincident(g736,g737)
    c: Coincident(g742,g743)
    c: Coincident(g876,g877)
    c: Coincident(g916,g917)
    c: Coincident(g915,g916)
    c: Coincident(g37,g38)
    c: Coincident(g20,g23)
    c: Coincident(g845,g846)
    c: Coincident(g824,g825)
    c: Coincident(g773,g774)
    c: Coincident(g892,g893)
    c: Coincident(g748,g749)
    c: Coincident(g735,g736)
    c: Coincident(g910,g911)
    c: Coincident(g757,g758)
    c: Coincident(g875,g876)
    c: Coincident(g908,g909)
    c: Coincident(g825,g826)
    c: Coincident(g844,g845)
    c: Coincident(g907,g908)
    c: Coincident(g909,g910)
    c: Coincident(g792,g793)
    c: Coincident(g22,g23)
    c: Coincident(g38,g39)
    c: Coincident(g823,g824)
    c: Coincident(g846,g847)
    c: Coincident(g893,g894)
    c: Coincident(g865,g866)
    c: Coincident(g840,g841)
    c: Coincident(g819,g820)
    c: Coincident(g863,g865)
    c: Coincident(g917,g918)
    c: Coincident(g793,g794)
    c: Coincident(g776,g777)
    c: Coincident(g841,g842)
    c: Coincident(g818,g819)
    c: Coincident(g734,g735)
    c: Coincident(g874,g875)
    c: Coincident(g906,g907)
    c: Coincident(g820,g821)
    c: Coincident(g839,g840)
    c: Coincident(g774,g775)
    c: Coincident(g791,g792)
    c: Coincident(g894,g895)
    c: Coincident(g756,g757)
    c: Coincident(g787,g788)
    c: Coincident(g786,g787)
    c: Coincident(g843,g844)
    c: Coincident(g826,g827)
    c: Coincident(g777,g778)
    c: Coincident(g874,g897)
    c: Coincident(g788,g789)
    c: Coincident(g867,g873)
    c: Coincident(g749,g750)
    c: Coincident(g842,g843)
    c: Coincident(g901,g902)
    c: Coincident(g817,g818)
    c: Coincident(g733,g734)
    c: Coincident(g902,g903)
    c: Coincident(g872,g873)
    c: Coincident(g775,g776)
    c: Coincident(g821,g822)
    c: Coincident(g822,g823)
    c: Coincident(g838,g839)
    c: Coincident(g847,g848)
    c: Coincident(g794,g795)
    c: Coincident(g905,g906)
    c: Coincident(g871,g872)
    c: Coincident(g895,g896)
    c: Coincident(g785,g786)
    c: Coincident(g755,g756)
    c: Coincident(g898,g918)
    c: Coincident(g752,g753)
    c: Coincident(g789,g790)
    c: Coincident(g790,g791)
    c: Coincident(g816,g817)
    c: Coincident(g827,g828)
    c: Coincident(g837,g838)
    c: Coincident(g750,g751)
    c: Coincident(g732,g733)
    c: Coincident(g848,g849)
    c: Coincident(g755,g778)
    c: Coincident(g896,g897)
    c: Coincident(g795,g796)
    c: Coincident(g784,g785)
    c: Coincident(g815,g816)
    c: Coincident(g900,g901)
    c: Coincident(g814,g815)
    c: Coincident(g904,g905)
    c: Coincident(g753,g754)
    c: Coincident(g903,g904)
    c: Coincident(g836,g837)
    c: Coincident(g828,g829)
    c: Coincident(g829,g830)
    c: Coincident(g751,g752)
    c: Coincident(g849,g850)
    c: Coincident(g783,g784)
    c: Coincident(g830,g831)
    c: Coincident(g796,g797)
    c: Coincident(g812,g813)
    c: Coincident(g835,g836)
    c: Coincident(g898,g899)
    c: Coincident(g813,g814)
    c: Coincident(g731,g732)
    c: Coincident(g899,g900)
    c: Coincident(g811,g812)
    c: Coincident(g782,g783)
    c: Coincident(g834,g835)
    c: Coincident(g731,g754)
    c: Coincident(g870,g871)
    c: Coincident(g850,g851)
    c: Coincident(g803,g831)
    c: Coincident(g810,g811)
    c: Coincident(g869,g870)
    c: Coincident(g864,g866)
    c: Coincident(g868,g869)
    c: Coincident(g833,g834)
    c: Coincident(g781,g782)
    c: Coincident(g797,g798)
    c: Coincident(g807,g808)
    c: Coincident(g867,g868)
    c: Coincident(g861,g863)
    c: Coincident(g851,g852)
    c: Coincident(g806,g807)
    c: Coincident(g859,g861)
    c: Coincident(g862,g864)
    c: Coincident(g809,g810)
    c: Coincident(g860,g862)
    c: Coincident(g780,g781)
    c: Coincident(g852,g853)
    c: Coincident(g856,g857)
    c: Coincident(g832,g833)
    c: Coincident(g798,g799)
    c: Coincident(g857,g859)
    c: Coincident(g24,g27)
    c: Coincident(g33,g34)
    c: Coincident(g808,g809)
    c: Coincident(g803,g804)
    c: Coincident(g853,g854)
    c: Coincident(g800,g801)
    c: Coincident(g26,g27)
    c: Coincident(g34,g35)
    c: Coincident(g832,g855)
    c: Coincident(g805,g806)
    c: Coincident(g799,g800)
    c: Coincident(g804,g805)
    c: Coincident(g779,g780)
    c: Coincident(g854,g855)
    c: Coincident(g801,g802)
    c: Coincident(g858,g860)
    c: Coincident(g856,g858)
    c: Coincident(g779,g802)
    c: Coincident(g28,g31)
    c: Coincident(g30,g31)
FEATURE [PartDesign::Pad] Pad007
  BaseFeature = -> Fillet011
  Direction = (0,0,-1)
  Length = 1.5
  Length2 = 10
  Profile = -> Sketch023
  ReferenceAxis = -> Sketch023 [N_Axis]
  Refine = true
  SideType = 0
  Suppressed = false
  Type = 0
  Type2 = 0
  expr: Length = 1.5
FEATURE [PartDesign::Body] Body022  label="desc_upper_ring"
  AllowCompound = false
  Group = -> [Sketch021,Pad006,Sketch022,Pocket006,PolarPattern005,Fillet010,Fillet011,Sketch023,Pad007]
  Origin = -> Origin036
  Tip = -> Pad007
COMPONENT P3 — recipe-attached ("motor_gear001", modeled in this document).
Construction recipe (the document's own serialized feature program — sketch geometry with constraints, then the solid features built on it; lengths are millimeters unless a unit is written):

FEATURE [PartDesign::FeaturePython] InvoluteGear001  # WARN: FeaturePython — macro-defined, semantics opaque (R4)
  AttacherType = Attacher::AttachEngine3D
  Suppressed = false
  addendum_diameter = 27
  angular_backlash = 0
  axle_hole = false
  axle_holesize = 10
  backlash = 0
  clearance = 0.25
  double_helix = false
  head = 0
  head_fillet = 0
  height = 5
  helix_angle = 0
  module = 1.5
  num_teeth = 16
  numpoints = 20
  offset_hole = false
  offset_holeoffset = 10
  offset_holesize = 10
  pitch_diameter = 24
  pressure_angle = 20
  properties_from_tool = false
  reversed_backlash = false
  root_diameter = 20.25
  root_fillet = 0
  shift = 0
  simple = false
  transverse_pitch = 4.71239
  traverse_module = 1.5
  undercut = false
  version = 1.3.0
  expr: angular_backlash = backlash / pitch_diameter * 360 ° / pi
  expr: module = 1.5
  expr: num_teeth = 16
FEATURE [Sketcher::SketchObject] Sketch008
  ArcFitTolerance = 1e-06
  AttachmentSupport = -> [InvoluteGear001]
  ExternalTypes = [0]
  FullyConstrained = true
  MakeInternals = false
  MapMode = 5
  Placement = pos=(0,0,5) rot=(0,0,1;0rad)
  expr: Constraints[11] = 3.1
  sketch-geometry (4):
    g0: ArcOfCircle CenterX=0 CenterY=0 CenterZ=0 NormalX=0 NormalY=0 NormalZ=1 AngleXU=0 Radius=2.5 StartAngle=2.47285 EndAngle=3.81034
    g1: ArcOfCircle CenterX=0 CenterY=0 CenterZ=0 NormalX=0 NormalY=0 NormalZ=1 AngleXU=0 Radius=2.5 StartAngle=5.61444 EndAngle=6.95193
    g2: LineSegment StartX=-1.9615 StartY=1.55 StartZ=0 EndX=1.9615 EndY=1.55 EndZ=0
    g3: LineSegment StartX=1.9615 StartY=-1.55 StartZ=0 EndX=-1.9615 EndY=-1.55 EndZ=0
  constraints (12):
    c: Coincident(g0,g-1)
    c: Coincident(g0,g1)
    c: Diameter(g0) = 5
    c: Equal(g1,g0)
    c: Coincident(g2,g0)
    c: Coincident(g2,g1)
    c: Coincident(g3,g1)
    c: Coincident(g3,g0)
    c: Parallel(g3,g2)
    c: Parallel(g-1,g2)
    c: Equal(g2,g3)
    c: Distance(g3,g2) = 3.1
FEATURE [PartDesign::Pocket] Pocket004
  BaseFeature = -> InvoluteGear001
  Direction = (0,0,-1)
  Length = 5
  Length2 = 5
  Profile = -> Sketch008
  ReferenceAxis = -> Sketch008 [N_Axis]
  Refine = true
  SideType = 0
  Suppressed = false
  Type = 0
  Type2 = 0
FEATURE [PartDesign::Fillet] Fillet012
  Base = -> Pocket004 [Face5,Face4]
  BaseFeature = -> Pocket004
  Radius = 0.25
  Refine = true
  SupportTransform = false
  Suppressed = false
  UseAllEdges = false
  expr: Radius = 0.25
FEATURE [PartDesign::Body] Body005  label="motor_gear001"
  AllowCompound = false
  Group = -> [InvoluteGear001,Sketch008,Pocket004,Fillet012]
  Origin = -> Origin010
  Placement = pos=(0,0,75) rot=(0,0,1;0rad)
  Tip = -> Fillet012
COMPONENT P4 — recipe-attached ("outer_gear", modeled in this document).
Construction recipe (the document's own serialized feature program — sketch geometry with constraints, then the solid features built on it; lengths are millimeters unless a unit is written):

FEATURE [PartDesign::FeaturePython] InternalInvoluteGear  # WARN: FeaturePython — macro-defined, semantics opaque (R4)
  AttacherType = Attacher::AttachEngine3D
  Suppressed = false
  addendum_diameter = 94.2
  angular_backlash = 0
  backlash = 0
  clearance = 0.2
  double_helix = false
  head = -0.4
  head_fillet = 0
  height = 5
  helix_angle = 0
  module = 1.5
  num_teeth = 64
  numpoints = 20
  outside_diameter = 106
  pitch_diameter = 96
  pressure_angle = 20
  properties_from_tool = false
  reversed_backlash = false
  root_diameter = 99.6
  root_fillet = 0
  shift = 0
  simple = false
  thickness = 5
  transverse_pitch = 4.71239
  version = 1.3.0
  expr: angular_backlash = backlash / pitch_diameter * 360 ° / pi
  expr: clearance = 0.2
  expr: module = 1.5
  expr: num_teeth = 64
  expr: pressure_angle = 20
FEATURE [Part::DatumPlane] DatumPlane002
  AttachmentSupport = -> [InternalInvoluteGear]
  MapMode = 7
  Placement = pos=(53,0,0) rot=(1,0,0;1.5708rad)
FEATURE [Sketcher::SketchObject] Sketch010
  ArcFitTolerance = 1e-06
  AttachmentSupport = -> [DatumPlane002]
  ExternalGeometry = -> [InternalInvoluteGear]
  ExternalTypes = [0]
  FullyConstrained = false
  MakeInternals = false
  MapMode = 5
  Placement = pos=(53,0,0) rot=(1,0,0;1.5708rad)
  expr: Constraints[10] = VarSet.outer_wall_thickness
  expr: Constraints[11] = VarSet.outer_wall_thickness
  expr: Constraints[14] = VarSet.outer_wall_thickness
  expr: Constraints[17] = VarSet.fillet_oouter_gear
  expr: Constraints[2] = 5
  expr: Constraints[34] = VarSet.outer_wall_thickness
  expr: Constraints[36] = VarSet.outer_ring_height
  expr: Constraints[37] = VarSet.fillet_oouter_gear
  expr: Constraints[38] = 30
  expr: Constraints[45] = VarSet.fillet_oouter_gear
  expr: Constraints[50] = 25
  expr: Constraints[52] = 10
  expr: Constraints[6] = 25
  expr: Constraints[9] = VarSet.outer_wall_thickness
  sketch-geometry (28):
    g0: LineSegment StartX=0 StartY=0 StartZ=0 EndX=0 EndY=5 EndZ=0
    g1: LineSegment StartX=0 StartY=0 StartZ=0 EndX=24.0192 EndY=0 EndZ=0
    g2: LineSegment StartX=25.6005 StartY=0.775418 StartZ=0 EndX=40.7862 EndY=20.3842 EndZ=0
    g3: LineSegment StartX=24.6198 StartY=2.77542 StartZ=0 EndX=39.2049 EndY=21.6088 EndZ=0
    g4: LineSegment StartX=9.57963 StartY=2 StartZ=0 EndX=23.0385 EndY=2 EndZ=0
    g5: LineSegment StartX=0 StartY=5 StartZ=0 EndX=-2 EndY=5 EndZ=0
    g6: LineSegment StartX=-0.122418 StartY=35.2036 StartZ=0 EndX=4.22e-14 EndY=7.67973 EndZ=0
    g7: LineSegment StartX=8.57963 StartY=2.26795 StartZ=0 EndX=0.399992 EndY=6.99046 EndZ=0
    g8: ArcOfCircle CenterX=0.799992 CenterY=7.68328 CenterZ=0 NormalX=0 NormalY=0 NormalZ=1 AngleXU=0 Radius=0.8 StartAngle=3.14604 EndAngle=4.18879
    g9: ArcOfCircle CenterX=9.57963 CenterY=4 CenterZ=0 NormalX=0 NormalY=0 NormalZ=1 AngleXU=0 Radius=2 StartAngle=4.18879 EndAngle=4.71239
    g10: GeomPoint [constr] X=9.04373 Y=2 Z=0
    g11: ArcOfCircle CenterX=23.0385 CenterY=4 CenterZ=0 NormalX=0 NormalY=0 NormalZ=1 AngleXU=0 Radius=2 StartAngle=4.71239 EndAngle=5.62423
    g12: GeomPoint [constr] X=24.0192 Y=2 Z=0
    g13: ArcOfCircle CenterX=24.0192 CenterY=2 CenterZ=0 NormalX=0 NormalY=0 NormalZ=1 AngleXU=0 Radius=2 StartAngle=4.71239 EndAngle=5.62423
    g14: GeomPoint [constr] X=25 Y=0 Z=0
    g15: GeomPoint [constr] X=29 Y=5.16508 Z=0
    g16: GeomPoint [constr] X=27 Y=5.84896 Z=0
    g17: ArcOfCircle CenterX=-0.92241 CenterY=35.2 CenterZ=0 NormalX=0 NormalY=0 NormalZ=1 AngleXU=0 Radius=0.8 StartAngle=0.00444768 EndAngle=1.5708
    g18: LineSegment StartX=-10.9224 StartY=36 StartZ=0 EndX=-5.92241 EndY=36 EndZ=0
    g19: ArcOfCircle CenterX=19.4391 CenterY=36.916 CenterZ=0 NormalX=0 NormalY=0 NormalZ=1 AngleXU=0 Radius=27 StartAngle=5.62423 EndAngle=6.21764
    g20: ArcOfCircle CenterX=19.4391 CenterY=36.916 CenterZ=0 NormalX=0 NormalY=0 NormalZ=1 AngleXU=0 Radius=25 StartAngle=5.62423 EndAngle=6.21662
    g21: ArcOfCircle CenterX=45.1819 CenterY=35.2 CenterZ=0 NormalX=0 NormalY=0 NormalZ=1 AngleXU=0 Radius=0.8 StartAngle=1.5708 EndAngle=3.07503
    g22: LineSegment StartX=45.5828 StartY=36 StartZ=0 EndX=45.1819 EndY=36 EndZ=0
    g23: ArcOfCircle CenterX=45.5828 CenterY=35.2 CenterZ=0 NormalX=0 NormalY=0 NormalZ=1 AngleXU=0 Radius=0.8 StartAngle=6.21764 EndAngle=7.85398
    g24: ArcOfCircle CenterX=-10.9224 CenterY=35.2 CenterZ=0 NormalX=0 NormalY=0 NormalZ=1 AngleXU=0 Radius=0.8 StartAngle=1.5708 EndAngle=3.66964
    g25: LineSegment StartX=-11.6134 StartY=34.7969 StartZ=0 EndX=-2.05968 EndY=18.418 EndZ=0
    g26: LineSegment StartX=-2.05968 StartY=18.418 StartZ=0 EndX=-2 EndY=5 EndZ=0
    g27: LineSegment StartX=-5.92241 StartY=36 StartZ=0 EndX=-0.92241 EndY=36 EndZ=0
  constraints (66):
    c: Coincident(g0,g-1)
    c: PointOnObject(g0,g-2)
    c: DistanceY(g0,g0) = 5
    c: Coincident(g1,g0)
    c: PointOnObject(g14,g-1)
    c: Parallel(g3,g2)
    c: DistanceX(g1,g14) = 25
    c: DistanceX(g14,g15) = 4
    c: Parallel(g4,g1)
    c: Distance(g1,g4) = 2
    c: DistanceX(g16,g15) = 2
    c: Distance(g14,g3) = 2
    c: Coincident(g5,g0)
    c: Horizontal(g5)
    c: DistanceX(g5,g5) = 2
    c: Tangent(g8,g7) = 1.5708
    c: Tangent(g8,g6) = -1.5708
    c: Radius(g8) = 0.8
    c: PointOnObject(g6,g-2)
    c: PointOnObject(g10,g7)
    c: PointOnObject(g10,g4)
    c: Tangent(g7,g9) = 1.5708
    c: Tangent(g4,g9) = -1.5708
    c: PointOnObject(g12,g4)
    c: PointOnObject(g12,g3)
    c: Tangent(g4,g11) = -1.5708
    c: Tangent(g3,g11) = -1.5708
    c: PointOnObject(g14,g1)
    c: PointOnObject(g14,g2)
    c: Tangent(g1,g13) = -1.5708
    c: Tangent(g2,g13) = -1.5708
    c: PointOnObject(g15,g2)
    c: PointOnObject(g16,g3)
    c: Equal(g13,g11)
    c: Distance(g0,g8) = 2
    c: Tangent(g17,g6) = 1.5708
    c: Distance(g18,g-1) = 36
    c: Radius(g17) = 0.8
    c: Angle(g7,g1) = 0.523599
    c: Equal(g11,g9)
    c: Coincident(g20,g19)
    c: Tangent(g20,g3) = -1.5708
    c: Tangent(g19,g2) = -1.5708
    c: Tangent(g22,g21) = -1.5708
    c: Tangent(g21,g20) = 1.5708
    c: Radius(g21) = 0.8
    c: Tangent(g23,g22) = -1.5708
    c: Tangent(g23,g19) = -1.5708
    c: Equal(g23,g21)
    c: Parallel(g22,g-1)
    c: Radius(g20) = 25
    c: Radius(g11) = 2
    c: DistanceX(g18,g27) = 10
    c: Tangent(g24,g18) = 1.5708
    c: Equal(g24,g17)
    c: Coincident(g26,g25)
    c: Coincident(g26,g5)
    c: Parallel(g26,g6)
    c: Tangent(g25,g24) = -1.5708
    c: Perpendicular(g-2,g18)
    c: Perpendicular(g-2,g27)
    c: Coincident(g18,g27)
    c: Tangent(g27,g17) = 1.5708
    c: Equal(g27,g18)
    c: Angle(g26,g25) = 0.523599
    c: Vertical(g18,g-3)
FEATURE [PartDesign::Revolution] Revolution001
  Angle = 360
  Angle2 = 60
  Axis = (1e-16,1e-16,1)
  Base = (0,0,0)
  BaseFeature = -> InternalInvoluteGear
  Profile = -> Sketch010
  ReferenceAxis = -> Z_Axis013
  Refine = true
  Reversed = true
  Suppressed = false
  Type = 0
FEATURE [Sketcher::SketchObject] Sketch011
  ArcFitTolerance = 1e-06
  AttachmentSupport = -> [DatumPlane002]
  ExternalGeometry = -> [Revolution001]
  ExternalTypes = [0,0,0,0,0,0,0,0,0]
  FullyConstrained = true
  MakeInternals = false
  MapMode = 5
  Placement = pos=(53,0,0) rot=(1,0,0;1.5708rad)
  sketch-geometry (2):
    g0: LineSegment StartX=-0.92241 StartY=36 StartZ=0 EndX=45.1819 EndY=36 EndZ=0
    g1: LineSegment StartX=9.57963 StartY=2 StartZ=0 EndX=23.0385 EndY=2 EndZ=0
  constraints (4):
    c: Coincident(g0,g-11)
    c: Coincident(g0,g-7)
    c: Tangent(g1,g-6) = -1.5708
    c: Coincident(g1,g-8)
FEATURE [PartDesign::Revolution] Revolution002
  Angle = 1
  Angle2 = 60
  Axis = (1e-16,1e-16,1)
  Base = (0,0,0)
  BaseFeature = -> Revolution001
  Midplane = true
  Profile = -> Sketch011
  ReferenceAxis = -> Z_Axis013
  Refine = true
  Suppressed = false
  Type = 0
  expr: Angle = 1
FEATURE [PartDesign::PolarPattern] PolarPattern
  Angle = 360
  Axis = -> Z_Axis013
  BaseFeature = -> Revolution002
  Mode = 0
  Occurrences = 32
  Offset = 120
  Originals = -> [Revolution002]
  Refine = true
  Suppressed = false
  TransformMode = 0
  expr: Occurrences = 32
FEATURE [Sketcher::SketchObject] Sketch015
  ArcFitTolerance = 1e-06
  AttachmentSupport = -> [PolarPattern]
  ExternalGeometry = -> [PolarPattern]
  ExternalTypes = [0,0,0]
  FullyConstrained = true
  MakeInternals = false
  MapMode = 5
  Placement = pos=(4e-15,4e-15,36) rot=(0,0,1;0rad)
  expr: Constraints[13] = 9
  sketch-geometry (5):
    g0: Circle [constr] CenterX=0 CenterY=0 CenterZ=0 NormalX=0 NormalY=0 NormalZ=1 AngleXU=0 Radius=52.0776
    g1: Circle CenterX=0 CenterY=0 CenterZ=0 NormalX=0 NormalY=0 NormalZ=1 AngleXU=0 Radius=42.5776
    g2: Circle CenterX=0 CenterY=0 CenterZ=0 NormalX=0 NormalY=0 NormalZ=1 AngleXU=0 Radius=51.5776
    g3: LineSegment [constr] StartX=-42.5776 StartY=0 StartZ=0 EndX=-42.0776 EndY=0 EndZ=0
    g4: LineSegment [constr] StartX=-52.0776 StartY=0 StartZ=0 EndX=-51.5776 EndY=0 EndZ=0
  constraints (14):
    c: Coincident(g0,g-3)
    c: PointOnObject(g-4,g0)
    c: Coincident(g1,g0)
    c: Coincident(g2,g0)
    c: PointOnObject(g3,g1)
    c: PointOnObject(g3,g-3)
    c: PointOnObject(g3,g-1)
    c: PointOnObject(g3,g-1)
    c: PointOnObject(g4,g0)
    c: PointOnObject(g4,g2)
    c: PointOnObject(g4,g-1)
    c: PointOnObject(g4,g-1)
    c: Equal(g4,g3)
    c: Distance(g2,g1) = 9
FEATURE [PartDesign::Pocket] Pocket005
  BaseFeature = -> PolarPattern
  Direction = (0,0,-1)
  Length = 3
  Length2 = 5
  Profile = -> Sketch015
  ReferenceAxis = -> Sketch015 [N_Axis]
  Refine = true
  SideType = 0
  Suppressed = false
  Type = 0
  Type2 = 0
  expr: Length = 3
FEATURE [PartDesign::Fillet] Fillet003
  Base = -> Pocket005 [Edge312,Edge949]
  BaseFeature = -> Pocket005
  Radius = 1
  Refine = true
  SupportTransform = false
  Suppressed = false
  UseAllEdges = false
  expr: Radius = 1
FEATURE [Sketcher::SketchObject] Sketch016
  ArcFitTolerance = 1e-06
  AttachmentSupport = -> [Fillet003]
  ExternalGeometry = -> [Fillet003]
  ExternalTypes = [0]
  FullyConstrained = false
  MakeInternals = false
  MapMode = 5
  Placement = pos=(0,0,33) rot=(0,0,1;0rad)
  sketch-geometry (8):
    g0: ArcOfCircle CenterX=4e-15 CenterY=4e-15 CenterZ=0 NormalX=0 NormalY=0 NormalZ=1 AngleXU=0 Radius=44.0776 StartAngle=1.01451 EndAngle=1.42895
    g1: ArcOfCircle CenterX=4e-15 CenterY=4e-15 CenterZ=0 NormalX=0 NormalY=0 NormalZ=1 AngleXU=0 Radius=50.0776 StartAngle=1.01451 EndAngle=1.42895
    g2: LineSegment StartX=6.23147 StartY=43.6349 StartZ=0 EndX=7.07972 EndY=49.5746 EndZ=0
    g3: LineSegment StartX=23.2744 StartY=37.4318 StartZ=0 EndX=26.4426 EndY=42.5271 EndZ=0
    g4: LineSegment [constr] StartX=23.2744 StartY=37.4318 StartZ=0 EndX=23.0104 EndY=37.0071 EndZ=0
    g5: LineSegment [constr] StartX=26.4426 StartY=42.5271 StartZ=0 EndX=26.7066 EndY=42.9517 EndZ=0
    g6: LineSegment [constr] StartX=4e-15 StartY=4e-15 StartZ=0 EndX=-40.9495 EndY=14.9044 EndZ=0
    g7: LineSegment [constr] StartX=4e-15 StartY=4e-15 StartZ=0 EndX=14.9044 EndY=40.9495 EndZ=0
  constraints (22):
    c: Coincident(g0,g-4)
    c: Coincident(g1,g0)
    c: Coincident(g2,g0)
    c: Coincident(g2,g1)
    c: Coincident(g3,g0)
    c: Coincident(g3,g1)
    c: Equal(g2,g3)
    c: Perpendicular(g0,g2)
    c: Coincident(g4,g0)
    c: PointOnObject(g4,g-4)
    c: Coincident(g5,g1)
    c: PointOnObject(g5,g-3)
    c: Parallel(g4,g3)
    c: Parallel(g3,g5)
    c: Equal(g5,g4)
    c: Distance(g3,g3) = 6
    c: Coincident(g6,g0)
    c: Angle(g6,g-1) = 0.349066
    c: PointOnObject(g6,g-4)
    c: Coincident(g7,g0)
    c: Perpendicular(g6,g7)
    c: Equal(g7,g6)
FEATURE [PartDesign::Pad] Pad004
  BaseFeature = -> Fillet003
  Direction = (0,0,1)
  Length = 1.5
  Length2 = 10
  Profile = -> Sketch016
  ReferenceAxis = -> Sketch016 [N_Axis]
  Refine = true
  SideType = 0
  Suppressed = false
  Type = 0
  Type2 = 0
  expr: Length = 1.5
FEATURE [PartDesign::PolarPattern] PolarPattern002
  Angle = 360
  Axis = -> Sketch016 [N_Axis]
  BaseFeature = -> Pad004
  Mode = 0
  Occurrences = 2
  Offset = 120
  Originals = -> [Pad004]
  Refine = true
  Suppressed = false
  TransformMode = 0
FEATURE [PartDesign::Fillet] Fillet004
  Base = -> PolarPattern002 [Face177,Face175]
  BaseFeature = -> PolarPattern002
  Radius = 1
  Refine = true
  SupportTransform = false
  Suppressed = false
  UseAllEdges = false
FEATURE [PartDesign::Body] Body016  label="outer_gear"
  AllowCompound = false
  Group = -> [InternalInvoluteGear,DatumPlane002,Sketch010,Revolution001,Sketch011,Revolution002,PolarPattern,Sketch015,Pocket005,Fillet003,Sketch016,Pad004,PolarPattern002,Fillet004]
  Origin = -> Origin026
  Placement = pos=(0,0,41) rot=(0,0,1;0rad)
  Tip = -> Fillet004
COMPONENT P5 — recipe-attached ("upper_cover_display", modeled in this document).
Construction recipe (the document's own serialized feature program — sketch geometry with constraints, then the solid features built on it; lengths are millimeters unless a unit is written):

FEATURE [Sketcher::SketchObject] Sketch012
  ArcFitTolerance = 1e-06
  AttachmentSupport = -> [Origin034]
  ExternalTypes = [0]
  FullyConstrained = true
  MakeInternals = false
  MapMode = 5
  expr: Constraints[2] = 80
  sketch-geometry (3):
    g0: Circle CenterX=0 CenterY=0 CenterZ=0 NormalX=0 NormalY=0 NormalZ=1 AngleXU=0 Radius=21
    g1: Circle CenterX=0 CenterY=0 CenterZ=0 NormalX=0 NormalY=0 NormalZ=1 AngleXU=0 Radius=40
    g2: Circle CenterX=0 CenterY=0 CenterZ=0 NormalX=0 NormalY=0 NormalZ=1 AngleXU=0 Radius=38.5
  constraints (6):
    c: Diameter(g0) = 42
    c: Coincident(g0,g-1)
    c: Diameter(g1) = 80
    c: Coincident(g1,g0)
    c: Coincident(g2,g0)
    c: Diameter(g2) = 77
FEATURE [PartDesign::Pad] Pad005
  Direction = (0,0,1)
  Length = 3
  Length2 = 10
  Profile = -> Sketch012 [Edge2,Edge1]
  ReferenceAxis = -> Sketch012 [N_Axis]
  Refine = true
  SideType = 0
  Suppressed = false
  Type = 0
  Type2 = 0
  expr: Length = 3
FEATURE [Part::DatumPlane] DatumPlane003
  AttachmentSupport = -> [Sketch012]
  MapMode = 7
  Placement = pos=(40,0,0) rot=(1,0,0;1.5708rad)
FEATURE [Sketcher::SketchObject] Sketch017
  ArcFitTolerance = 1e-06
  AttachmentSupport = -> [DatumPlane003]
  ExternalTypes = [0]
  FullyConstrained = true
  MakeInternals = false
  MapMode = 5
  Placement = pos=(40,0,0) rot=(1,0,0;1.5708rad)
  expr: Constraints[4] = 14
  sketch-geometry (6):
    g0: LineSegment StartX=5.78797 StartY=-27 StartZ=0 EndX=5.78797 EndY=-13 EndZ=0
    g1: LineSegment StartX=5.78797 StartY=-13 StartZ=0 EndX=0 EndY=0 EndZ=0
    g2: LineSegment StartX=0 StartY=0 StartZ=0 EndX=-1.5 EndY=0 EndZ=0
    g3: LineSegment StartX=-1.5 StartY=0 StartZ=0 EndX=4.28797 EndY=-13 EndZ=0
    g4: LineSegment StartX=4.28797 StartY=-13 StartZ=0 EndX=4.28797 EndY=-27 EndZ=0
    g5: LineSegment StartX=4.28797 StartY=-27 StartZ=0 EndX=5.78797 EndY=-27 EndZ=0
  constraints (17):
    c: Vertical(g0)
    c: Coincident(g1,g0)
    c: Coincident(g1,g-1)
    c: Angle(g0,g1) = 0.418879
    c: DistanceY(g0,g0) = 14
    c: DistanceY(g0,g1) = 27
    c: Coincident(g2,g1)
    c: PointOnObject(g2,g-1)
    c: Coincident(g2,g3)
    c: Coincident(g3,g4)
    c: Vertical(g4)
    c: Coincident(g4,g5)
    c: Coincident(g5,g0)
    c: Perpendicular(g4,g5)
    c: Equal(g3,g1)
    c: Parallel(g3,g1)
    c: DistanceX(g5,g5) = 1.5
FEATURE [PartDesign::Revolution] Revolution003
  Angle = 360
  Angle2 = 60
  Axis = (1e-16,1e-16,1)
  Base = (0,0,0)
  BaseFeature = -> Pad005
  Profile = -> Sketch017
  ReferenceAxis = -> Z_Axis017
  Refine = true
  Reversed = true
  Suppressed = false
  Type = 0
FEATURE [PartDesign::Chamfer] Chamfer
  Angle = 45
  Base = -> Revolution003 [Edge13,Edge10]
  BaseFeature = -> Revolution003
  ChamferType = 0
  FlipDirection = false
  Refine = true
  Size = 2
  Size2 = 1
  SupportTransform = false
  Suppressed = false
  UseAllEdges = false
FEATURE [Part::DatumPlane] DatumPlane004
  AttachmentSupport = -> [Chamfer]
  MapMode = 7
  Placement = pos=(44.288,-6.1e-15,-27) rot=(0,0.707107,0.707107;3.14159rad)
FEATURE [Sketcher::SketchObject] Sketch018
  ArcFitTolerance = 1e-06
  AttachmentSupport = -> [DatumPlane004]
  ExternalTypes = [0]
  FullyConstrained = true
  MakeInternals = false
  MapMode = 5
  Placement = pos=(44.288,-6.1e-15,-27) rot=(0,0.707107,0.707107;3.14159rad)
  sketch-geometry (4):
    g0: LineSegment StartX=0 StartY=0 StartZ=0 EndX=0 EndY=5.12132 EndZ=0
    g1: LineSegment StartX=0 StartY=5.12132 StartZ=0 EndX=2.12132 EndY=3 EndZ=0
    g2: LineSegment StartX=2.12132 StartY=3 StartZ=0 EndX=2.12132 EndY=0 EndZ=0
    g3: LineSegment StartX=2.12132 StartY=0 StartZ=0 EndX=0 EndY=0 EndZ=0
  constraints (11):
    c: Coincident(g-1,g0)
    c: Vertical(g0)
    c: Coincident(g0,g1)
    c: Coincident(g1,g2)
    c: PointOnObject(g2,g-1)
    c: Vertical(g2)
    c: Coincident(g2,g3)
    c: Coincident(g3,g0)
    c: Angle(g2,g1) = 0.785398
    c: Equal(g2,g1)
    c: DistanceY(g2,g2) = 3
FEATURE [PartDesign::Revolution] Revolution004
  Angle = 9
  Angle2 = 60
  Axis = (1e-16,1e-16,1)
  Base = (0,0,0)
  BaseFeature = -> Chamfer
  Profile = -> Sketch018
  ReferenceAxis = -> Z_Axis017
  Refine = true
  Suppressed = false
  Type = 0
  expr: Angle = 9
FEATURE [PartDesign::PolarPattern] PolarPattern003
  Angle = 360
  Axis = -> Z_Axis017
  BaseFeature = -> Revolution004
  Mode = 0
  Occurrences = 4
  Offset = 120
  Originals = -> [Revolution004]
  Refine = true
  Suppressed = false
  TransformMode = 0
FEATURE [PartDesign::Fillet] Fillet009
  Base = -> PolarPattern003 [Face21,Face22,Face23,Face7]
  BaseFeature = -> PolarPattern003
  Radius = 0.5
  Refine = true
  SupportTransform = false
  Suppressed = false
  UseAllEdges = false
  expr: Radius = 0.5
FEATURE [PartDesign::Body] Body021  label="upper_cover_display"
  AllowCompound = false
  Group = -> [Sketch012,Pad005,DatumPlane003,Sketch017,Revolution003,Chamfer,DatumPlane004,Sketch018,Revolution004,PolarPattern003,Fillet009]
  Origin = -> Origin034
  Tip = -> Fillet009
PROVENANCE & LICENSES
A FreeCAD (.FCStd) document from a public repository crawl; recipes are the document's own serialized feature recipes (and, for linked parts, companion documents' recipes).
License: mit.
